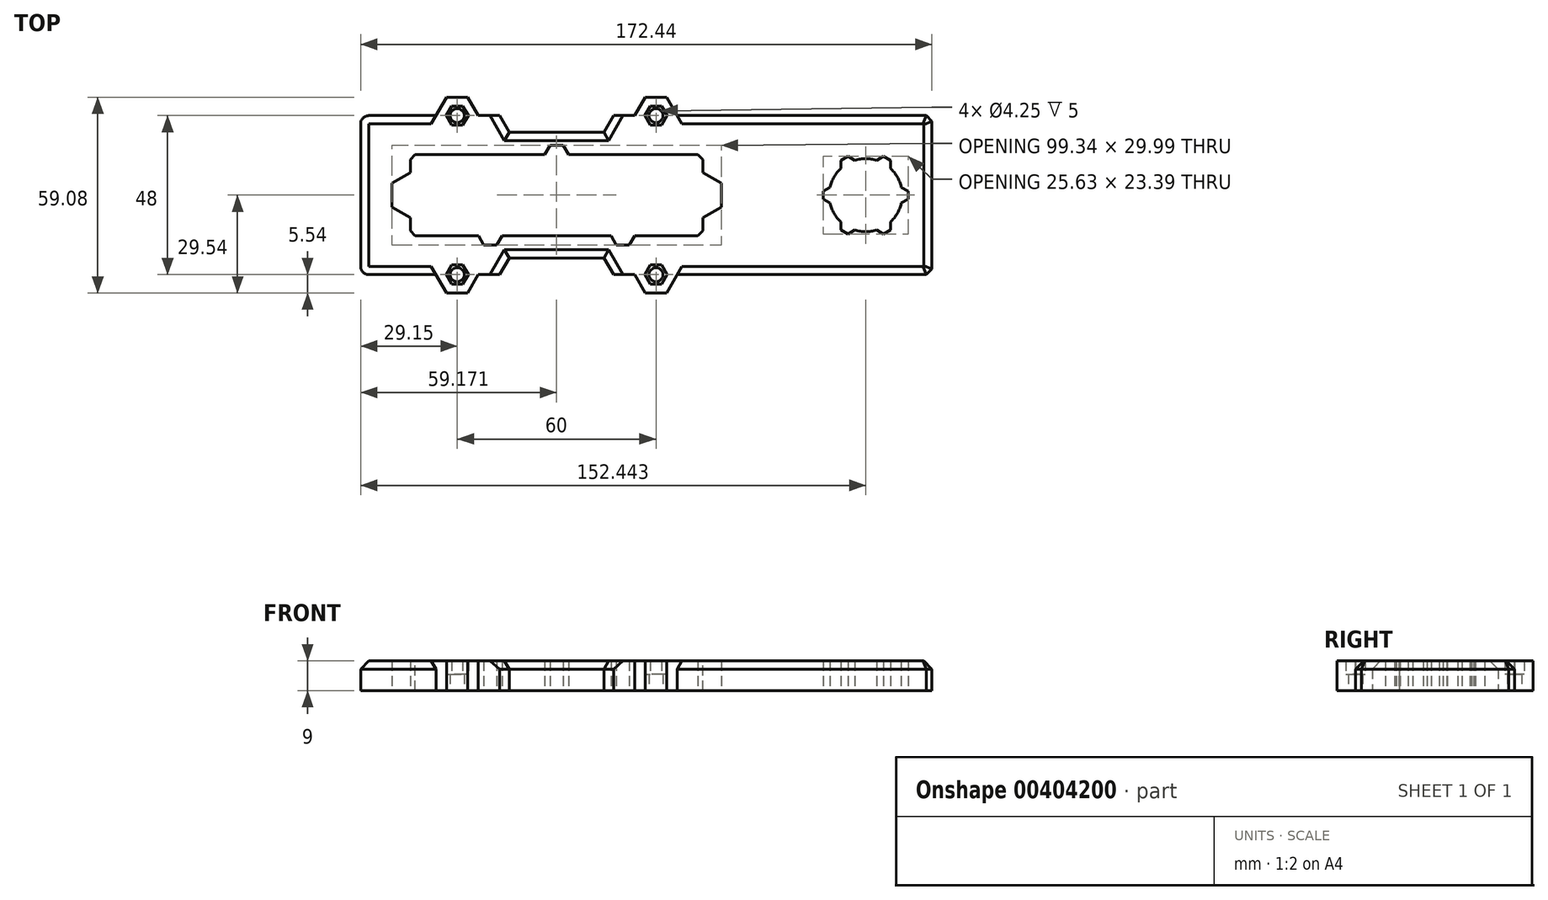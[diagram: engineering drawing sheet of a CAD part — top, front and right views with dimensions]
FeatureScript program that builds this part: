
annotation { "Feature Type Name" : "Feature", "Feature Type Description" : "" }
export const myFeature = defineFeature(function(context is Context, id is Id, definition is map)
    precondition{}
    {
        {
            var Q0;
            Q0=qCreatedBy(makeId("Top.planeOp"),FACE);
            var sketch = newSketch(context, id + "F0", { "sketchPlane" : qUnion([Q0])});
            skLineSegment(sketch, "E0.bottom", {"start": v(37.5, 8.37) * mm, "end": v(-37.5, 8.37) * mm, "construction": true});
            skLineSegment(sketch, "E0.top", {"start": v(37.5, -8.37) * mm, "end": v(-37.5, -8.37) * mm, "construction": true});
            skLineSegment(sketch, "E0.left", {"start": v(37.5, 8.37) * mm, "end": v(37.5, -8.37) * mm, "construction": true});
            skLineSegment(sketch, "E0.right", {"start": v(-37.5, 8.37) * mm, "end": v(-37.5, -8.37) * mm, "construction": true});
            skPoint(sketch, "E0.middle", {"position": v(0, 0) * mm});
            skLineSegment(sketch, "E1.bottom", {"start": v(43.5, 11.57) * mm, "end": v(2.77, 11.57) * mm, "construction": true});
            skLineSegment(sketch, "E1.top", {"start": v(43.5, -11.57) * mm, "end": v(23.2, -11.57) * mm, "construction": true});
            skLineSegment(sketch, "E1.left", {"start": v(43.5, 11.57) * mm, "end": v(43.5, 5.54) * mm, "construction": true});
            skLineSegment(sketch, "E1.right", {"start": v(-43.5, 11.57) * mm, "end": v(-43.5, 6.4) * mm, "construction": true});
            skCircle(sketch, "E2.cCircle", {"center": v(43.5, 0) * mm, "radius": 5.54 * mm, "construction": true});
            skPoint(sketch, "E2.cCircle.centerSnap0", {"position": v(43.5, 0) * mm});
            skLineSegment(sketch, "E2.0", {"start": v(49.04, 3.2) * mm, "end": v(49.04, -3.2) * mm, "construction": true});
            skLineSegment(sketch, "E2.1", {"start": v(49.04, -3.2) * mm, "end": v(43.5, -6.4) * mm, "construction": true});
            skLineSegment(sketch, "E2.2", {"start": v(43.5, -6.4) * mm, "end": v(37.96, -3.2) * mm, "construction": true});
            skLineSegment(sketch, "E2.3", {"start": v(37.96, -3.2) * mm, "end": v(37.96, 3.2) * mm, "construction": true});
            skLineSegment(sketch, "E2.4", {"start": v(37.96, 3.2) * mm, "end": v(43.5, 6.4) * mm, "construction": true});
            skLineSegment(sketch, "E2.5", {"start": v(43.5, 6.4) * mm, "end": v(49.04, 3.2) * mm, "construction": true});
            skPoint(sketch, "E2.0.midPoint", {"position": v(49.04, 0) * mm});
            skLineSegment(sketch, "E3.MirrorCS", {"start": v(-43.5, 6.4) * mm, "end": v(-49.04, 3.2) * mm, "construction": true});
            skLineSegment(sketch, "E4.MirrorCS", {"start": v(-49.04, 3.2) * mm, "end": v(-49.04, -3.2) * mm, "construction": true});
            skLineSegment(sketch, "E5.MirrorCS", {"start": v(-49.04, -3.2) * mm, "end": v(-43.5, -6.4) * mm, "construction": true});
            skLineSegment(sketch, "E6.trimOffspring", {"start": v(-43.5, -6.4) * mm, "end": v(-43.5, -11.57) * mm, "construction": true});
            skLineSegment(sketch, "E7.trimOffspring", {"start": v(43.5, -5.54) * mm, "end": v(43.5, -11.57) * mm, "construction": true});
            skCircle(sketch, "E8.cCircle", {"center": v(0, 11.57) * mm, "radius": 2.77 * mm, "construction": true});
            skLineSegment(sketch, "E8.0", {"start": v(-1.6, 14.35) * mm, "end": v(1.6, 14.35) * mm, "construction": true});
            skLineSegment(sketch, "E8.1", {"start": v(1.6, 14.35) * mm, "end": v(3.2, 11.57) * mm, "construction": true});
            skLineSegment(sketch, "E8.2", {"start": v(3.2, 11.57) * mm, "end": v(1.6, 8.8) * mm, "construction": true});
            skLineSegment(sketch, "E8.3", {"start": v(1.6, 8.8) * mm, "end": v(-1.6, 8.8) * mm, "construction": true});
            skLineSegment(sketch, "E8.4", {"start": v(-1.6, 8.8) * mm, "end": v(-3.2, 11.57) * mm, "construction": true});
            skLineSegment(sketch, "E8.5", {"start": v(-3.2, 11.57) * mm, "end": v(-1.6, 14.35) * mm, "construction": true});
            skPoint(sketch, "E8.0.midPoint", {"position": v(0, 14.35) * mm});
            skCircle(sketch, "E9.cCircle", {"center": v(-20, -11.57) * mm, "radius": 2.77 * mm, "construction": true});
            skLineSegment(sketch, "E9.0", {"start": v(-18.4, -14.35) * mm, "end": v(-21.6, -14.35) * mm, "construction": true});
            skLineSegment(sketch, "E9.1", {"start": v(-21.6, -14.35) * mm, "end": v(-23.2, -11.57) * mm, "construction": true});
            skLineSegment(sketch, "E9.2", {"start": v(-23.2, -11.57) * mm, "end": v(-21.6, -8.8) * mm, "construction": true});
            skLineSegment(sketch, "E9.3", {"start": v(-21.6, -8.8) * mm, "end": v(-18.4, -8.8) * mm, "construction": true});
            skLineSegment(sketch, "E9.4", {"start": v(-18.4, -8.8) * mm, "end": v(-16.8, -11.57) * mm, "construction": true});
            skLineSegment(sketch, "E9.5", {"start": v(-16.8, -11.57) * mm, "end": v(-18.4, -14.35) * mm, "construction": true});
            skPoint(sketch, "E9.0.midPoint", {"position": v(-20, -14.35) * mm});
            skLineSegment(sketch, "E10.MirrorCS", {"start": v(16.8, -11.57) * mm, "end": v(18.4, -14.35) * mm, "construction": true});
            skLineSegment(sketch, "E11.MirrorCS", {"start": v(21.6, -14.35) * mm, "end": v(23.2, -11.57) * mm, "construction": true});
            skLineSegment(sketch, "E12.MirrorCS", {"start": v(18.4, -14.35) * mm, "end": v(21.6, -14.35) * mm, "construction": true});
            skLineSegment(sketch, "E13.trimOffspring", {"start": v(16.8, -11.57) * mm, "end": v(-17.23, -11.57) * mm, "construction": true});
            skLineSegment(sketch, "E14.trimOffspring", {"start": v(-22.77, -11.57) * mm, "end": v(-43.5, -11.57) * mm, "construction": true});
            skLineSegment(sketch, "E15.trimOffspring", {"start": v(-2.77, 11.57) * mm, "end": v(-43.5, 11.57) * mm, "construction": true});
            skCircle(sketch, "E16", {"center": v(43.5, 0) * mm, "radius": 2.25 * mm, "construction": true});
            skCircle(sketch, "E17.MirrorC", {"center": v(-43.5, 0) * mm, "radius": 2.25 * mm, "construction": true});
            skLineSegment(sketch, "E18", {"start": v(0, 15) * mm, "end": v(-1.98, 15) * mm});
            skLineSegment(sketch, "E19", {"start": v(-1.98, 15) * mm, "end": v(-3.58, 12.22) * mm});
            skLineSegment(sketch, "E20", {"start": v(-3.58, 12.22) * mm, "end": v(-44.15, 12.22) * mm});
            skLineSegment(sketch, "E21", {"start": v(-44.15, 12.22) * mm, "end": v(-44.15, 6.78) * mm});
            skLineSegment(sketch, "E22", {"start": v(-44.15, 6.78) * mm, "end": v(-49.7, 3.58) * mm});
            skLineSegment(sketch, "E23", {"start": v(-49.7, 3.58) * mm, "end": v(-49.7, 0) * mm});
            skLineSegment(sketch, "E24.MirrorCS", {"start": v(0, 15) * mm, "end": v(1.98, 15) * mm});
            skLineSegment(sketch, "E25.MirrorCS", {"start": v(1.98, 15) * mm, "end": v(3.58, 12.22) * mm});
            skLineSegment(sketch, "E26.MirrorCS", {"start": v(3.58, 12.22) * mm, "end": v(44.15, 12.22) * mm});
            skLineSegment(sketch, "E27.MirrorCS", {"start": v(44.15, 12.22) * mm, "end": v(44.15, 6.78) * mm});
            skLineSegment(sketch, "E28.MirrorCS", {"start": v(44.15, 6.78) * mm, "end": v(49.7, 3.58) * mm});
            skLineSegment(sketch, "E29.MirrorCS", {"start": v(49.7, 3.58) * mm, "end": v(49.7, 0) * mm});
            skLineSegment(sketch, "E30.MirrorCS", {"start": v(-49.7, -3.58) * mm, "end": v(-49.7, 0) * mm});
            skLineSegment(sketch, "E31.MirrorCS", {"start": v(-44.15, -6.78) * mm, "end": v(-49.7, -3.58) * mm});
            skLineSegment(sketch, "E32.MirrorCS", {"start": v(-44.15, -12.22) * mm, "end": v(-44.15, -6.78) * mm});
            skLineSegment(sketch, "E33.MirrorCS", {"start": v(-3.58, -12.22) * mm, "end": v(-16.42, -12.22) * mm});
            skLineSegment(sketch, "E34.MirrorCS", {"start": v(-1.98, -15) * mm, "end": v(-3.58, -12.22) * mm, "construction": true});
            skLineSegment(sketch, "E35.MirrorCS", {"start": v(0, -15) * mm, "end": v(-1.98, -15) * mm, "construction": true});
            skLineSegment(sketch, "E36.MirrorCS", {"start": v(0, -15) * mm, "end": v(1.98, -15) * mm, "construction": true});
            skLineSegment(sketch, "E37.MirrorCS", {"start": v(1.98, -15) * mm, "end": v(3.58, -12.22) * mm, "construction": true});
            skLineSegment(sketch, "E38.MirrorCS", {"start": v(3.58, -12.22) * mm, "end": v(16.42, -12.22) * mm});
            skLineSegment(sketch, "E39.MirrorCS", {"start": v(44.15, -12.22) * mm, "end": v(44.15, -6.78) * mm});
            skLineSegment(sketch, "E40.MirrorCS", {"start": v(44.15, -6.78) * mm, "end": v(49.7, -3.58) * mm});
            skLineSegment(sketch, "E41.MirrorCS", {"start": v(49.7, -3.58) * mm, "end": v(49.7, 0) * mm});
            skLineSegment(sketch, "E42", {"start": v(-23.58, -12.23) * mm, "end": v(-21.98, -15) * mm});
            skLineSegment(sketch, "E43", {"start": v(-21.98, -15) * mm, "end": v(-18.02, -15) * mm});
            skLineSegment(sketch, "E44", {"start": v(-18.02, -15) * mm, "end": v(-16.42, -12.23) * mm});
            skLineSegment(sketch, "E45.MirrorCS", {"start": v(18.02, -15) * mm, "end": v(16.42, -12.23) * mm});
            skLineSegment(sketch, "E46.MirrorCS", {"start": v(23.58, -12.23) * mm, "end": v(21.98, -15) * mm});
            skLineSegment(sketch, "E47.MirrorCS", {"start": v(21.98, -15) * mm, "end": v(18.02, -15) * mm});
            skLineSegment(sketch, "E48", {"start": v(-3.58, -12.22) * mm, "end": v(3.58, -12.22) * mm});
            skLineSegment(sketch, "E49.trimOffspring", {"start": v(-23.58, -12.22) * mm, "end": v(-44.15, -12.22) * mm});
            skLineSegment(sketch, "E50.trimOffspring", {"start": v(23.58, -12.22) * mm, "end": v(44.15, -12.22) * mm});
            skLineSegment(sketch, "E51", {"start": v(0, -14.23) * mm, "end": v(-15.27, -14.23) * mm});
            skLineSegment(sketch, "E52", {"start": v(-15.27, -14.23) * mm, "end": v(-16.87, -17) * mm});
            skLineSegment(sketch, "E53", {"start": v(-16.87, -17) * mm, "end": v(-23.13, -17) * mm});
            skLineSegment(sketch, "E54", {"start": v(-23.13, -17) * mm, "end": v(-24.73, -14.23) * mm});
            skLineSegment(sketch, "E55", {"start": v(-24.73, -14.23) * mm, "end": v(-46.15, -14.23) * mm});
            skLineSegment(sketch, "E56", {"start": v(-46.15, -14.23) * mm, "end": v(-46.15, -7.93) * mm, "construction": true});
            skLineSegment(sketch, "E57", {"start": v(-46.15, -7.93) * mm, "end": v(-51.7, -4.73) * mm, "construction": true});
            skLineSegment(sketch, "E58", {"start": v(-51.7, -4.73) * mm, "end": v(-51.7, 4.73) * mm, "construction": true});
            skLineSegment(sketch, "E59", {"start": v(-51.7, 4.73) * mm, "end": v(-46.15, 7.93) * mm, "construction": true});
            skLineSegment(sketch, "E60", {"start": v(-46.15, 7.93) * mm, "end": v(-46.15, 14.22) * mm, "construction": true});
            skLineSegment(sketch, "E61", {"start": v(-46.15, 14.22) * mm, "end": v(-4.73, 14.22) * mm});
            skLineSegment(sketch, "E62", {"start": v(-4.73, 14.22) * mm, "end": v(-3.13, 17) * mm});
            skLineSegment(sketch, "E63", {"start": v(-3.13, 17) * mm, "end": v(0, 17) * mm});
            skLineSegment(sketch, "E64.MirrorCS", {"start": v(0, -14.23) * mm, "end": v(15.27, -14.23) * mm});
            skLineSegment(sketch, "E65.MirrorCS", {"start": v(15.27, -14.23) * mm, "end": v(16.87, -17) * mm});
            skLineSegment(sketch, "E66.MirrorCS", {"start": v(16.87, -17) * mm, "end": v(23.13, -17) * mm});
            skLineSegment(sketch, "E67.MirrorCS", {"start": v(23.13, -17) * mm, "end": v(24.73, -14.23) * mm});
            skLineSegment(sketch, "E68.MirrorCS", {"start": v(24.73, -14.23) * mm, "end": v(46.15, -14.23) * mm});
            skLineSegment(sketch, "E69.MirrorCS", {"start": v(46.15, -14.23) * mm, "end": v(46.15, -7.93) * mm});
            skLineSegment(sketch, "E70.MirrorCS", {"start": v(46.15, -7.93) * mm, "end": v(51.7, -4.73) * mm});
            skLineSegment(sketch, "E71.MirrorCS", {"start": v(51.7, -4.73) * mm, "end": v(51.7, 4.73) * mm});
            skLineSegment(sketch, "E72.MirrorCS", {"start": v(51.7, 4.73) * mm, "end": v(46.15, 7.93) * mm});
            skLineSegment(sketch, "E73.MirrorCS", {"start": v(46.15, 7.93) * mm, "end": v(46.15, 14.22) * mm});
            skLineSegment(sketch, "E74.MirrorCS", {"start": v(46.15, 14.22) * mm, "end": v(4.73, 14.22) * mm});
            skLineSegment(sketch, "E75.MirrorCS", {"start": v(4.73, 14.22) * mm, "end": v(3.13, 17) * mm});
            skLineSegment(sketch, "E76.MirrorCS", {"start": v(3.13, 17) * mm, "end": v(0, 17) * mm});
            skLineSegment(sketch, "E77", {"start": v(-46.15, 14.22) * mm, "end": v(-54.15, 14.22) * mm});
            skLineSegment(sketch, "E78", {"start": v(-54.15, 14.22) * mm, "end": v(-54.15, -14.23) * mm});
            skLineSegment(sketch, "E79", {"start": v(-54.15, -14.23) * mm, "end": v(-46.15, -14.23) * mm});
            skSolve(sketch);
        }
        {
            var Q0;
            Q0=qSketchRegion(id+"F0",true);
            extrude(context, id + "F1", {"entities" : qUnion([Q0]), "depth" : 36.5 * mm});
        }
        {
            var Q0;
            Q0=makeQuery(id+"F1.opExtrude","SWEPT_EDGE",EDGE,{"disambiguationData":[OSD([sQuery(id+"F0.wireOp",EDGE,"E20"),sQuery(id+"F0.wireOp",EDGE,"E21")])]});
            var Q1;
            Q1=makeQuery(id+"F1.opExtrude","SWEPT_EDGE",EDGE,{"disambiguationData":[OSD([sQuery(id+"F0.wireOp",EDGE,"E26.MirrorCS"),sQuery(id+"F0.wireOp",EDGE,"E27.MirrorCS")])]});
            var Q2;
            Q2=makeQuery(id+"F1.opExtrude","SWEPT_EDGE",EDGE,{"disambiguationData":[OSD([sQuery(id+"F0.wireOp",EDGE,"E39.MirrorCS"),sQuery(id+"F0.wireOp",EDGE,"E50.trimOffspring")])]});
            var Q3;
            Q3=makeQuery(id+"F1.opExtrude","SWEPT_EDGE",EDGE,{"disambiguationData":[OSD([sQuery(id+"F0.wireOp",EDGE,"E32.MirrorCS"),sQuery(id+"F0.wireOp",EDGE,"E49.trimOffspring")])]});
            chamfer(context, id + "F2", {"entities" : qUnion([Q0, Q1, Q2, Q3]), "width" : 1.5 * mm, "tangentPropagation" : true});
        }
        {
            var Q0;
            Q0=qCreatedBy(makeId("Right.planeOp"),FACE);
            var sketch = newSketch(context, id + "F3", { "sketchPlane" : qUnion([Q0])});
            skArc(sketch, "E80", {"start": v(-11, 32.75) * mm, "mid": v(0, 21.75) * mm, "end": v(11, 32.75) * mm});
            skLineSegment(sketch, "E81", {"start": v(-11, 32.75) * mm, "end": v(-11, 36.5) * mm});
            skLineSegment(sketch, "E82", {"start": v(-11, 36.5) * mm, "end": v(-10.34, 36.5) * mm});
            skLineSegment(sketch, "E83.MirrorCS", {"start": v(11, 32.75) * mm, "end": v(11, 36.5) * mm});
            skArc(sketch, "E84.trimOffspring", {"start": v(10.34, 36.5) * mm, "mid": v(0, 43.75) * mm, "end": v(-10.34, 36.5) * mm});
            skLineSegment(sketch, "E85", {"start": v(10.34, 36.5) * mm, "end": v(11, 36.5) * mm});
            skSolve(sketch);
        }
        {
            var Q0;
            Q0=qSketchRegion(id+"F3",true);
            extrude(context, id + "F4", {"entities" : qUnion([Q0]), "operationType" : NewBodyOperationType.REMOVE, "endBound" : BoundingType.SYMMETRIC, "oppositeDirection" : true, "depth" : 150 * mm});
        }
        {
            var Q0;
            Q0=makeQuery(id+"F1.opExtrude","SWEPT_FACE",FACE,{"disambiguationData":[OSD([sQuery(id+"F0.wireOp",EDGE,"E78")])]});
            var sketch = newSketch(context, id + "F5", { "sketchPlane" : qUnion([Q0])});
            skLineSegment(sketch, "E86", {"start": v(-14.22, 36.5) * mm, "end": v(-14.22, 0) * mm, "construction": true});
            skLineSegment(sketch, "E87", {"start": v(-14.22, 0) * mm, "end": v(14.23, 0) * mm});
            skLineSegment(sketch, "E88", {"start": v(14.23, 0) * mm, "end": v(14.23, 36.5) * mm, "construction": true});
            skArc(sketch, "E89", {"start": v(11, 32.75) * mm, "mid": v(0, 21.75) * mm, "end": v(-11, 32.75) * mm});
            skCircle(sketch, "E90.cCircle", {"center": v(18, 14.75) * mm, "radius": 2.92 * mm, "construction": true});
            skLineSegment(sketch, "E90.0", {"start": v(20.92, 16.43) * mm, "end": v(20.92, 13.07) * mm});
            skLineSegment(sketch, "E90.1", {"start": v(20.92, 13.07) * mm, "end": v(18, 11.38) * mm});
            skLineSegment(sketch, "E90.2", {"start": v(18, 11.38) * mm, "end": v(15.08, 13.07) * mm});
            skLineSegment(sketch, "E90.3", {"start": v(15.08, 13.07) * mm, "end": v(15.08, 16.43) * mm});
            skLineSegment(sketch, "E90.4", {"start": v(15.08, 16.43) * mm, "end": v(18, 18.12) * mm});
            skLineSegment(sketch, "E90.5", {"start": v(18, 18.12) * mm, "end": v(20.92, 16.43) * mm});
            skPoint(sketch, "E90.0.midPoint", {"position": v(20.92, 14.75) * mm});
            skLineSegment(sketch, "E91.MirrorCS", {"start": v(-15.08, 13.07) * mm, "end": v(-15.08, 16.43) * mm});
            skLineSegment(sketch, "E92.MirrorCS", {"start": v(-18, 11.38) * mm, "end": v(-15.08, 13.07) * mm});
            skLineSegment(sketch, "E93.MirrorCS", {"start": v(-20.92, 13.07) * mm, "end": v(-18, 11.38) * mm});
            skLineSegment(sketch, "E94.MirrorCS", {"start": v(-20.92, 16.43) * mm, "end": v(-20.92, 13.07) * mm});
            skCircle(sketch, "E95.MirrorC", {"center": v(-18, 14.75) * mm, "radius": 2.92 * mm, "construction": true});
            skLineSegment(sketch, "E96.MirrorCS", {"start": v(-15.08, 16.43) * mm, "end": v(-18, 18.12) * mm});
            skLineSegment(sketch, "E97.MirrorCS", {"start": v(-18, 18.12) * mm, "end": v(-20.92, 16.43) * mm});
            skPoint(sketch, "E98.MirrorP", {"position": v(-20.92, 14.75) * mm});
            skLineSegment(sketch, "E99", {"start": v(-14.22, 0) * mm, "end": v(-24, 0) * mm});
            skLineSegment(sketch, "E100", {"start": v(-24, 0) * mm, "end": v(-24, 32.75) * mm});
            skLineSegment(sketch, "E101.MirrorCS", {"start": v(24, 0) * mm, "end": v(24, 32.75) * mm});
            skLineSegment(sketch, "E102.MirrorCS", {"start": v(14.22, 0) * mm, "end": v(24, 0) * mm});
            skArc(sketch, "E103", {"start": v(11, 32.75) * mm, "mid": v(0, 43.75) * mm, "end": v(-11, 32.75) * mm});
            skCircle(sketch, "E104.cCircle", {"center": v(0, 50.75) * mm, "radius": 2.92 * mm, "construction": true});
            skLineSegment(sketch, "E104.0", {"start": v(2.92, 52.43) * mm, "end": v(2.92, 49.07) * mm});
            skLineSegment(sketch, "E104.1", {"start": v(2.92, 49.07) * mm, "end": v(0, 47.38) * mm});
            skLineSegment(sketch, "E104.2", {"start": v(0, 47.38) * mm, "end": v(-2.92, 49.07) * mm});
            skLineSegment(sketch, "E104.3", {"start": v(-2.92, 49.07) * mm, "end": v(-2.92, 52.43) * mm});
            skLineSegment(sketch, "E104.4", {"start": v(-2.92, 52.43) * mm, "end": v(0, 54.12) * mm});
            skLineSegment(sketch, "E104.5", {"start": v(0, 54.12) * mm, "end": v(2.92, 52.43) * mm});
            skPoint(sketch, "E104.0.midPoint", {"position": v(2.92, 50.75) * mm});
            skArc(sketch, "E105", {"start": v(24, 32.75) * mm, "mid": v(0, 56.75) * mm, "end": v(-24, 32.75) * mm});
            skSolve(sketch);
        }
        {
            var Q0;
            Q0=qSketchRegion(id+"F5",true);
            extrude(context, id + "F6", {"entities" : qUnion([Q0]), "operationType" : NewBodyOperationType.ADD, "oppositeDirection" : true, "depth" : 4.5 * mm});
        }
        {
            var Q0;
            {var subQ0=sQuery(id+"F5.wireOp",EDGE,"E90.3");var subQ1=sQuery(id+"F5.wireOp",EDGE,"E90.2");var subQ2=sQuery(id+"F5.wireOp",EDGE,"E90.0");var subQ3=sQuery(id+"F5.wireOp",EDGE,"21dbecbc-3e90-4e6d-8c2d-dcc7a88c41760.MirrorCS");var subQ4=sQuery(id+"F5.wireOp",EDGE,"7LxXvKuB-2ogT-G9F5-G1mv-J76seeRdzQWf");var subQ5=sQuery(id+"F5.wireOp",EDGE,"E90.4");var subQ59=sQuery(id+"F5.wireOp",EDGE,"E90.1");var subQ60=sQuery(id+"F5.wireOp",EDGE,"E102.MirrorCS");var subQ61=sQuery(id+"F5.wireOp",EDGE,"E99");var subQ62=sQuery(id+"F5.wireOp",EDGE,"E87");var subQ63=sQuery(id+"F5.wireOp",EDGE,"E101.MirrorCS");var subQ64=sQuery(id+"F5.wireOp",EDGE,"E90.5");Q0=makeQuery(id+"F6.boolean.opBoolean","SPLIT",FACE,{"disambiguationData":[TD([makeQuery(id+"F6.opExtrude","SWEPT_FACE",FACE,{"disambiguationData":[OSD([subQ2])]})])],"derivedFrom":makeQuery(id+"F6.opExtrude","CAP_FACE",FACE,{"disambiguationData":[OSD([sQuery(id+"F5.wireOp",EDGE,"b1FAA0cU-aVsy-Hviu-uORb-ThKFGoumFDh2"),sQuery(id+"F5.wireOp",EDGE,"2LK7XLYA-R4sY-Yq1R-9r0a-fteJpxcb9tpt"),subQ62,subQ4,sQuery(id+"F5.wireOp",EDGE,"kGSWCWjE-YfoX-ZzYT-cJHE-sSvaP37tbrIv"),sQuery(id+"F5.wireOp",EDGE,"E89"),subQ2,subQ59,subQ1,subQ0,subQ5,subQ64,sQuery(id+"F5.wireOp",EDGE,"E91.MirrorCS"),sQuery(id+"F5.wireOp",EDGE,"E92.MirrorCS"),sQuery(id+"F5.wireOp",EDGE,"E93.MirrorCS"),sQuery(id+"F5.wireOp",EDGE,"E94.MirrorCS"),sQuery(id+"F5.wireOp",EDGE,"E96.MirrorCS"),sQuery(id+"F5.wireOp",EDGE,"E97.MirrorCS"),subQ61,sQuery(id+"F5.wireOp",EDGE,"E100"),sQuery(id+"F5.wireOp",EDGE,"KSvhVgnx-WBJf-5fod-QVyl-tOGzJuIU2zdj"),subQ3,subQ63,subQ60])],"isStart":false})});}
            var sketch = newSketch(context, id + "F7", { "sketchPlane" : qUnion([Q0])});
            skCircle(sketch, "E106.cCircle", {"center": v(-18, 14.75) * mm, "radius": 2.92 * mm, "construction": true});
            skPoint(sketch, "E106.cCircle.perimeterSnap0", {"position": v(-20.92, 14.75) * mm});
            skLineSegment(sketch, "E106.0", {"start": v(-20.92, 13.07) * mm, "end": v(-20.92, 16.43) * mm});
            skLineSegment(sketch, "E106.1", {"start": v(-20.92, 16.43) * mm, "end": v(-18, 18.12) * mm});
            skLineSegment(sketch, "E106.2", {"start": v(-18, 18.12) * mm, "end": v(-15.08, 16.43) * mm});
            skLineSegment(sketch, "E106.3", {"start": v(-15.08, 16.43) * mm, "end": v(-15.08, 13.07) * mm});
            skLineSegment(sketch, "E106.4", {"start": v(-15.08, 13.07) * mm, "end": v(-18, 11.38) * mm, "construction": true});
            skLineSegment(sketch, "E106.5", {"start": v(-18, 11.38) * mm, "end": v(-20.92, 13.07) * mm, "construction": true});
            skPoint(sketch, "E106.0.midPoint", {"position": v(-20.92, 14.75) * mm});
            skPoint(sketch, "E106.0.midPoint.positionSnap0", {"position": v(-20.92, 14.75) * mm});
            skLineSegment(sketch, "E107.MirrorCS", {"start": v(20.92, 13.07) * mm, "end": v(20.92, 16.43) * mm});
            skCircle(sketch, "E108.MirrorC", {"center": v(18, 14.75) * mm, "radius": 2.92 * mm, "construction": true});
            skLineSegment(sketch, "E109.MirrorCS", {"start": v(18, 11.38) * mm, "end": v(20.92, 13.07) * mm, "construction": true});
            skLineSegment(sketch, "E110.MirrorCS", {"start": v(15.08, 13.07) * mm, "end": v(18, 11.38) * mm, "construction": true});
            skLineSegment(sketch, "E111.MirrorCS", {"start": v(15.08, 16.43) * mm, "end": v(15.08, 13.07) * mm});
            skLineSegment(sketch, "E112.MirrorCS", {"start": v(20.92, 16.43) * mm, "end": v(18, 18.12) * mm});
            skPoint(sketch, "E113.MirrorP", {"position": v(20.92, 14.75) * mm});
            skLineSegment(sketch, "E114.MirrorCS", {"start": v(18, 18.12) * mm, "end": v(15.08, 16.43) * mm});
            skLineSegment(sketch, "E115.bottom", {"start": v(-24, 32.75) * mm, "end": v(-14.22, 32.75) * mm});
            skLineSegment(sketch, "E115.top", {"start": v(-24, 0) * mm, "end": v(-20.92, 0) * mm});
            skLineSegment(sketch, "E115.left", {"start": v(-24, 32.75) * mm, "end": v(-24, 0) * mm});
            skLineSegment(sketch, "E115.right", {"start": v(-14.22, 32.75) * mm, "end": v(-14.22, 0) * mm});
            skLineSegment(sketch, "E116.MirrorCS", {"start": v(24, 32.75) * mm, "end": v(14.23, 32.75) * mm});
            skLineSegment(sketch, "E117.MirrorCS", {"start": v(24, 32.75) * mm, "end": v(24, 0) * mm});
            skLineSegment(sketch, "E118.MirrorCS", {"start": v(14.23, 32.75) * mm, "end": v(14.23, 0) * mm});
            skLineSegment(sketch, "E119.MirrorCS", {"start": v(24, 0) * mm, "end": v(20.92, 0) * mm});
            skLineSegment(sketch, "E120", {"start": v(-20.92, 13.07) * mm, "end": v(-20.92, 0) * mm});
            skLineSegment(sketch, "E121", {"start": v(-15.08, 13.07) * mm, "end": v(-15.08, 0) * mm});
            skLineSegment(sketch, "E122.MirrorCS", {"start": v(15.08, 13.07) * mm, "end": v(15.08, 0) * mm});
            skLineSegment(sketch, "E123.MirrorCS", {"start": v(20.92, 13.07) * mm, "end": v(20.92, 0) * mm});
            skLineSegment(sketch, "E124.trimOffspring", {"start": v(-15.08, 0) * mm, "end": v(-14.22, 0) * mm});
            skLineSegment(sketch, "E125.trimOffspring", {"start": v(15.08, 0) * mm, "end": v(14.23, 0) * mm});
            skSolve(sketch);
        }
        {
            var Q0;
            Q0=qSketchRegion(id+"F7",true);
            extrude(context, id + "F8", {"entities" : qUnion([Q0]), "operationType" : NewBodyOperationType.ADD, "depth" : 4 * mm});
        }
        {
            var Q0;
            Q0=makeQuery(id+"F6.boolean.opBoolean","MERGE",FACE,{"derivedFrom":[makeQuery(id+"F1.opExtrude","SWEPT_FACE",FACE,{"disambiguationData":[OSD([sQuery(id+"F0.wireOp",EDGE,"E78")])]}),makeQuery(id+"F6.opExtrude","CAP_FACE",FACE,{"disambiguationData":[OSD([sQuery(id+"F5.wireOp",EDGE,"b1FAA0cU-aVsy-Hviu-uORb-ThKFGoumFDh2"),sQuery(id+"F5.wireOp",EDGE,"2LK7XLYA-R4sY-Yq1R-9r0a-fteJpxcb9tpt"),sQuery(id+"F5.wireOp",EDGE,"E87"),sQuery(id+"F5.wireOp",EDGE,"7LxXvKuB-2ogT-G9F5-G1mv-J76seeRdzQWf"),sQuery(id+"F5.wireOp",EDGE,"kGSWCWjE-YfoX-ZzYT-cJHE-sSvaP37tbrIv"),sQuery(id+"F5.wireOp",EDGE,"E89"),sQuery(id+"F5.wireOp",EDGE,"E90.0"),sQuery(id+"F5.wireOp",EDGE,"E90.1"),sQuery(id+"F5.wireOp",EDGE,"E90.2"),sQuery(id+"F5.wireOp",EDGE,"E90.3"),sQuery(id+"F5.wireOp",EDGE,"E90.4"),sQuery(id+"F5.wireOp",EDGE,"E90.5"),sQuery(id+"F5.wireOp",EDGE,"E91.MirrorCS"),sQuery(id+"F5.wireOp",EDGE,"E92.MirrorCS"),sQuery(id+"F5.wireOp",EDGE,"E93.MirrorCS"),sQuery(id+"F5.wireOp",EDGE,"E94.MirrorCS"),sQuery(id+"F5.wireOp",EDGE,"E96.MirrorCS"),sQuery(id+"F5.wireOp",EDGE,"E97.MirrorCS"),sQuery(id+"F5.wireOp",EDGE,"E99"),sQuery(id+"F5.wireOp",EDGE,"E100"),sQuery(id+"F5.wireOp",EDGE,"KSvhVgnx-WBJf-5fod-QVyl-tOGzJuIU2zdj"),sQuery(id+"F5.wireOp",EDGE,"21dbecbc-3e90-4e6d-8c2d-dcc7a88c41760.MirrorCS"),sQuery(id+"F5.wireOp",EDGE,"E101.MirrorCS"),sQuery(id+"F5.wireOp",EDGE,"E102.MirrorCS")])],"isStart":true})]});
            var sketch = newSketch(context, id + "F9", { "sketchPlane" : qUnion([Q0])});
            skCircle(sketch, "E126.cCircle", {"center": v(18, 14.75) * mm, "radius": 2.92 * mm, "construction": true});
            skLineSegment(sketch, "E126.0", {"start": v(20.92, 16.43) * mm, "end": v(20.92, 13.07) * mm});
            skLineSegment(sketch, "E126.1", {"start": v(20.92, 13.07) * mm, "end": v(18, 11.38) * mm, "construction": true});
            skLineSegment(sketch, "E126.2", {"start": v(18, 11.38) * mm, "end": v(15.08, 13.07) * mm, "construction": true});
            skLineSegment(sketch, "E126.3", {"start": v(15.08, 13.07) * mm, "end": v(15.08, 16.43) * mm});
            skLineSegment(sketch, "E126.4", {"start": v(15.08, 16.43) * mm, "end": v(18, 18.12) * mm});
            skLineSegment(sketch, "E126.5", {"start": v(18, 18.12) * mm, "end": v(20.92, 16.43) * mm});
            skPoint(sketch, "E126.0.midPoint", {"position": v(20.92, 14.75) * mm});
            skCircle(sketch, "E127", {"center": v(18, 14.75) * mm, "radius": 2.12 * mm});
            skLineSegment(sketch, "E128.MirrorCS", {"start": v(-20.92, 13.07) * mm, "end": v(-18, 11.38) * mm, "construction": true});
            skPoint(sketch, "E129.MirrorP", {"position": v(-20.92, 14.75) * mm});
            skCircle(sketch, "E130.MirrorC", {"center": v(-18, 14.75) * mm, "radius": 2.92 * mm, "construction": true});
            skCircle(sketch, "E131.MirrorC", {"center": v(-18, 14.75) * mm, "radius": 2.12 * mm});
            skLineSegment(sketch, "E132.MirrorCS", {"start": v(-18, 18.12) * mm, "end": v(-20.92, 16.43) * mm});
            skLineSegment(sketch, "E133.MirrorCS", {"start": v(-15.08, 16.43) * mm, "end": v(-18, 18.12) * mm});
            skLineSegment(sketch, "E134.MirrorCS", {"start": v(-15.08, 13.07) * mm, "end": v(-15.08, 16.43) * mm});
            skLineSegment(sketch, "E135.MirrorCS", {"start": v(-18, 11.38) * mm, "end": v(-15.08, 13.07) * mm, "construction": true});
            skLineSegment(sketch, "E136.MirrorCS", {"start": v(-20.92, 16.43) * mm, "end": v(-20.92, 13.07) * mm});
            skLineSegment(sketch, "E137", {"start": v(20.92, 13.07) * mm, "end": v(20.92, 0) * mm});
            skLineSegment(sketch, "E138", {"start": v(20.92, 0) * mm, "end": v(15.08, 0) * mm});
            skLineSegment(sketch, "E139", {"start": v(15.08, 0) * mm, "end": v(15.08, 13.07) * mm});
            skLineSegment(sketch, "E140.MirrorCS", {"start": v(-15.08, 0) * mm, "end": v(-15.08, 13.07) * mm});
            skLineSegment(sketch, "E141.MirrorCS", {"start": v(-20.92, 13.07) * mm, "end": v(-20.92, 0) * mm});
            skLineSegment(sketch, "E142.MirrorCS", {"start": v(-20.92, 0) * mm, "end": v(-15.08, 0) * mm});
            skSolve(sketch);
        }
        {
            var Q0;
            Q0=qSketchRegion(id+"F9",true);
            extrude(context, id + "F10", {"entities" : qUnion([Q0]), "operationType" : NewBodyOperationType.ADD, "oppositeDirection" : true, "depth" : 4 * mm});
        }
        {
            var Q0;
            {var subQ0=sQuery(id+"F5.wireOp",EDGE,"E100");var subQ1=sQuery(id+"F5.wireOp",EDGE,"E97.MirrorCS");var subQ2=sQuery(id+"F5.wireOp",EDGE,"E96.MirrorCS");var subQ3=sQuery(id+"F5.wireOp",EDGE,"E94.MirrorCS");var subQ4=sQuery(id+"F5.wireOp",EDGE,"E93.MirrorCS");var subQ5=sQuery(id+"F5.wireOp",EDGE,"E92.MirrorCS");var subQ6=sQuery(id+"F5.wireOp",EDGE,"E91.MirrorCS");var subQ7=sQuery(id+"F5.wireOp",EDGE,"E90.5");var subQ8=sQuery(id+"F5.wireOp",EDGE,"E90.4");var subQ9=sQuery(id+"F5.wireOp",EDGE,"E90.3");var subQ10=sQuery(id+"F5.wireOp",EDGE,"E90.2");var subQ11=sQuery(id+"F5.wireOp",EDGE,"E90.1");var subQ14=sQuery(id+"F5.wireOp",EDGE,"E104.0");var subQ73=sQuery(id+"F5.wireOp",EDGE,"E102.MirrorCS");var subQ74=sQuery(id+"F5.wireOp",EDGE,"E99");var subQ75=sQuery(id+"F5.wireOp",EDGE,"E87");var subQ76=sQuery(id+"F5.wireOp",EDGE,"822r9Sqc-ou8d-xyd6-ONRq-5U1WncNYngyn");var subQ77=sQuery(id+"F5.wireOp",EDGE,"E90.0");var subQ78=sQuery(id+"F5.wireOp",EDGE,"E103");var subQ79=sQuery(id+"F5.wireOp",EDGE,"E89");var subQ80=sQuery(id+"F5.wireOp",EDGE,"E101.MirrorCS");var subQ81=sQuery(id+"F5.wireOp",EDGE,"E104.1");var subQ82=sQuery(id+"F5.wireOp",EDGE,"E104.2");var subQ83=sQuery(id+"F5.wireOp",EDGE,"E104.3");var subQ84=sQuery(id+"F5.wireOp",EDGE,"E104.4");var subQ85=sQuery(id+"F5.wireOp",EDGE,"E104.5");Q0=makeQuery(id+"F6.boolean.opBoolean","SPLIT",FACE,{"disambiguationData":[TD([makeQuery(id+"F6.opExtrude","SWEPT_FACE",FACE,{"disambiguationData":[OSD([subQ77])]})])],"derivedFrom":makeQuery(id+"F6.opExtrude","CAP_FACE",FACE,{"disambiguationData":[OSD([subQ75,subQ79,subQ77,subQ11,subQ10,subQ9,subQ8,subQ7,subQ6,subQ5,subQ4,subQ3,subQ2,subQ1,subQ74,subQ0,subQ80,subQ73,subQ78,subQ76,subQ14,subQ81,subQ82,subQ83,subQ84,subQ85])],"isStart":false})});}
            var sketch = newSketch(context, id + "F11", { "sketchPlane" : qUnion([Q0])});
            skArc(sketch, "E143", {"start": v(-11, 32.75) * mm, "mid": v(0, 43.75) * mm, "end": v(11, 32.75) * mm});
            skArc(sketch, "E144", {"start": v(-24, 32.75) * mm, "mid": v(-17.97, 48.66) * mm, "end": v(-2.92, 56.57) * mm});
            skCircle(sketch, "E145.cCircle", {"center": v(0, 50.75) * mm, "radius": 2.92 * mm, "construction": true});
            skPoint(sketch, "E145.cCircle.perimeterSnap0", {"position": v(2.92, 50.75) * mm});
            skLineSegment(sketch, "E145.0", {"start": v(2.92, 52.43) * mm, "end": v(2.92, 49.07) * mm});
            skLineSegment(sketch, "E145.1", {"start": v(2.92, 49.07) * mm, "end": v(0, 47.38) * mm});
            skLineSegment(sketch, "E145.2", {"start": v(0, 47.38) * mm, "end": v(-2.92, 49.07) * mm});
            skLineSegment(sketch, "E145.3", {"start": v(-2.92, 49.07) * mm, "end": v(-2.92, 52.43) * mm});
            skLineSegment(sketch, "E145.4", {"start": v(-2.92, 52.43) * mm, "end": v(0, 54.12) * mm, "construction": true});
            skLineSegment(sketch, "E145.5", {"start": v(0, 54.12) * mm, "end": v(2.92, 52.43) * mm, "construction": true});
            skPoint(sketch, "E145.0.midPoint", {"position": v(2.92, 50.75) * mm});
            skPoint(sketch, "E145.0.midPoint.positionSnap0", {"position": v(2.92, 50.75) * mm});
            skLineSegment(sketch, "E146", {"start": v(-11, 32.75) * mm, "end": v(-24, 32.75) * mm});
            skLineSegment(sketch, "E147", {"start": v(11, 32.75) * mm, "end": v(24, 32.75) * mm});
            skLineSegment(sketch, "E148", {"start": v(-2.92, 56.57) * mm, "end": v(-2.92, 52.43) * mm});
            skLineSegment(sketch, "E149.MirrorCS", {"start": v(2.92, 56.57) * mm, "end": v(2.92, 52.43) * mm});
            skArc(sketch, "E150.trimOffspring", {"start": v(2.92, 56.57) * mm, "mid": v(17.97, 48.66) * mm, "end": v(24, 32.75) * mm});
            skSolve(sketch);
        }
        {
            var Q0;
            Q0=qSketchRegion(id+"F11",true);
            extrude(context, id + "F12", {"entities" : qUnion([Q0]), "operationType" : NewBodyOperationType.ADD, "depth" : 4 * mm});
        }
        {
            var Q0;
            Q0=makeQuery(id+"F10.boolean.opBoolean","MERGE",FACE,{"derivedFrom":[makeQuery(id+"F6.boolean.opBoolean","MERGE",FACE,{"derivedFrom":[makeQuery(id+"F1.opExtrude","SWEPT_FACE",FACE,{"disambiguationData":[OSD([sQuery(id+"F0.wireOp",EDGE,"E78")])]}),makeQuery(id+"F6.opExtrude","CAP_FACE",FACE,{"disambiguationData":[OSD([sQuery(id+"F5.wireOp",EDGE,"E87"),sQuery(id+"F5.wireOp",EDGE,"E89"),sQuery(id+"F5.wireOp",EDGE,"E90.0"),sQuery(id+"F5.wireOp",EDGE,"E90.1"),sQuery(id+"F5.wireOp",EDGE,"E90.2"),sQuery(id+"F5.wireOp",EDGE,"E90.3"),sQuery(id+"F5.wireOp",EDGE,"E90.4"),sQuery(id+"F5.wireOp",EDGE,"E90.5"),sQuery(id+"F5.wireOp",EDGE,"E91.MirrorCS"),sQuery(id+"F5.wireOp",EDGE,"E92.MirrorCS"),sQuery(id+"F5.wireOp",EDGE,"E93.MirrorCS"),sQuery(id+"F5.wireOp",EDGE,"E94.MirrorCS"),sQuery(id+"F5.wireOp",EDGE,"E96.MirrorCS"),sQuery(id+"F5.wireOp",EDGE,"E97.MirrorCS"),sQuery(id+"F5.wireOp",EDGE,"E99"),sQuery(id+"F5.wireOp",EDGE,"E100"),sQuery(id+"F5.wireOp",EDGE,"E101.MirrorCS"),sQuery(id+"F5.wireOp",EDGE,"E102.MirrorCS"),sQuery(id+"F5.wireOp",EDGE,"E103"),sQuery(id+"F5.wireOp",EDGE,"822r9Sqc-ou8d-xyd6-ONRq-5U1WncNYngyn"),sQuery(id+"F5.wireOp",EDGE,"E104.0"),sQuery(id+"F5.wireOp",EDGE,"E104.1"),sQuery(id+"F5.wireOp",EDGE,"E104.2"),sQuery(id+"F5.wireOp",EDGE,"E104.3"),sQuery(id+"F5.wireOp",EDGE,"E104.4"),sQuery(id+"F5.wireOp",EDGE,"E104.5")])],"isStart":true})]}),makeQuery(id+"F10.opExtrude","CAP_FACE",FACE,{"disambiguationData":[OSD([sQuery(id+"F9.wireOp",EDGE,"E126.0"),sQuery(id+"F9.wireOp",EDGE,"E126.1"),sQuery(id+"F9.wireOp",EDGE,"E126.2"),sQuery(id+"F9.wireOp",EDGE,"E126.3"),sQuery(id+"F9.wireOp",EDGE,"E126.4"),sQuery(id+"F9.wireOp",EDGE,"E126.5"),sQuery(id+"F9.wireOp",EDGE,"E127")])],"isStart":true}),makeQuery(id+"F10.opExtrude","CAP_FACE",FACE,{"disambiguationData":[OSD([sQuery(id+"F9.wireOp",EDGE,"E128.MirrorCS"),sQuery(id+"F9.wireOp",EDGE,"E131.MirrorC"),sQuery(id+"F9.wireOp",EDGE,"E132.MirrorCS"),sQuery(id+"F9.wireOp",EDGE,"E133.MirrorCS"),sQuery(id+"F9.wireOp",EDGE,"E134.MirrorCS"),sQuery(id+"F9.wireOp",EDGE,"E135.MirrorCS"),sQuery(id+"F9.wireOp",EDGE,"E136.MirrorCS")])],"isStart":true})]});
            var sketch = newSketch(context, id + "F13", { "sketchPlane" : qUnion([Q0])});
            skCircle(sketch, "E151.cCircle", {"center": v(0, 50.75) * mm, "radius": 2.92 * mm, "construction": true});
            skLineSegment(sketch, "E151.0", {"start": v(2.92, 52.43) * mm, "end": v(2.92, 49.07) * mm});
            skLineSegment(sketch, "E151.1", {"start": v(2.92, 49.07) * mm, "end": v(0, 47.38) * mm});
            skLineSegment(sketch, "E151.2", {"start": v(0, 47.38) * mm, "end": v(-2.92, 49.07) * mm});
            skLineSegment(sketch, "E151.3", {"start": v(-2.92, 49.07) * mm, "end": v(-2.92, 52.43) * mm});
            skLineSegment(sketch, "E151.4", {"start": v(-2.92, 52.43) * mm, "end": v(0, 54.12) * mm});
            skLineSegment(sketch, "E151.5", {"start": v(0, 54.12) * mm, "end": v(2.92, 52.43) * mm});
            skPoint(sketch, "E151.0.midPoint", {"position": v(2.92, 50.75) * mm});
            skCircle(sketch, "E152", {"center": v(0, 50.75) * mm, "radius": 2.12 * mm});
            skSolve(sketch);
        }
        {
            var Q0;
            Q0=qSketchRegion(id+"F13",true);
            extrude(context, id + "F14", {"entities" : qUnion([Q0]), "operationType" : NewBodyOperationType.ADD, "oppositeDirection" : true, "depth" : 4 * mm});
        }
        {
            var Q0;
            {var subQ0=sQuery(id+"F5.wireOp",EDGE,"E90.3");var subQ2=sQuery(id+"F5.wireOp",EDGE,"E90.2");var subQ58=sQuery(id+"F5.wireOp",EDGE,"E102.MirrorCS");var subQ59=sQuery(id+"F5.wireOp",EDGE,"E99");var subQ60=sQuery(id+"F5.wireOp",EDGE,"E87");var subQ62=sQuery(id+"F5.wireOp",EDGE,"E90.0");var subQ63=makeQuery(id+"F6.opExtrude","SWEPT_FACE",FACE,{"disambiguationData":[OSD([subQ62])]});var subQ64=sQuery(id+"F5.wireOp",EDGE,"E90.1");var subQ66=sQuery(id+"F5.wireOp",EDGE,"E100");var subQ67=sQuery(id+"F5.wireOp",EDGE,"E97.MirrorCS");var subQ68=sQuery(id+"F5.wireOp",EDGE,"E96.MirrorCS");var subQ69=sQuery(id+"F5.wireOp",EDGE,"E94.MirrorCS");var subQ70=sQuery(id+"F5.wireOp",EDGE,"E93.MirrorCS");var subQ71=sQuery(id+"F5.wireOp",EDGE,"E92.MirrorCS");var subQ72=sQuery(id+"F5.wireOp",EDGE,"E91.MirrorCS");var subQ73=sQuery(id+"F5.wireOp",EDGE,"E90.5");var subQ74=sQuery(id+"F5.wireOp",EDGE,"E90.4");var subQ75=sQuery(id+"F5.wireOp",EDGE,"E104.1");var subQ83=sQuery(id+"F5.wireOp",EDGE,"E104.0");var subQ84=sQuery(id+"F5.wireOp",EDGE,"E103");var subQ85=sQuery(id+"F5.wireOp",EDGE,"E89");var subQ86=sQuery(id+"F5.wireOp",EDGE,"E101.MirrorCS");var subQ87=sQuery(id+"F5.wireOp",EDGE,"E104.2");var subQ88=sQuery(id+"F5.wireOp",EDGE,"E104.3");var subQ89=sQuery(id+"F5.wireOp",EDGE,"E104.4");var subQ90=sQuery(id+"F5.wireOp",EDGE,"E104.5");var subQ91=sQuery(id+"F5.wireOp",EDGE,"E105");Q0=makeQuery(id+"F8.boolean.opBoolean","SPLIT",FACE,{"disambiguationData":[TD([subQ63])],"derivedFrom":makeQuery(id+"F6.boolean.opBoolean","SPLIT",FACE,{"disambiguationData":[TD([subQ63])],"derivedFrom":makeQuery(id+"F6.opExtrude","CAP_FACE",FACE,{"disambiguationData":[OSD([subQ60,subQ85,subQ62,subQ64,subQ2,subQ0,subQ74,subQ73,subQ72,subQ71,subQ70,subQ69,subQ68,subQ67,subQ59,subQ66,subQ86,subQ58,subQ84,subQ83,subQ75,subQ87,subQ88,subQ89,subQ90,subQ91])],"isStart":false})})});}
            var sketch = newSketch(context, id + "F15", { "sketchPlane" : qUnion([Q0])});
            skCircle(sketch, "E153.cCircle", {"center": v(-18, 14.75) * mm, "radius": 2.92 * mm, "construction": true});
            skLineSegment(sketch, "E153.0", {"start": v(-20.92, 13.07) * mm, "end": v(-20.92, 16.43) * mm});
            skLineSegment(sketch, "E153.1", {"start": v(-20.92, 16.43) * mm, "end": v(-18, 18.12) * mm});
            skLineSegment(sketch, "E153.2", {"start": v(-18, 18.12) * mm, "end": v(-15.08, 16.43) * mm});
            skLineSegment(sketch, "E153.3", {"start": v(-15.08, 16.43) * mm, "end": v(-15.08, 13.07) * mm});
            skLineSegment(sketch, "E153.4", {"start": v(-15.08, 13.07) * mm, "end": v(-18, 11.38) * mm});
            skLineSegment(sketch, "E153.5", {"start": v(-18, 11.38) * mm, "end": v(-20.92, 13.07) * mm});
            skPoint(sketch, "E153.0.midPoint", {"position": v(-20.92, 14.75) * mm});
            skCircle(sketch, "E154", {"center": v(-18, 14.75) * mm, "radius": 2.12 * mm});
            skCircle(sketch, "E155.MirrorC", {"center": v(18, 14.75) * mm, "radius": 2.92 * mm, "construction": true});
            skPoint(sketch, "E156.MirrorP", {"position": v(20.92, 14.75) * mm});
            skLineSegment(sketch, "E157.MirrorCS", {"start": v(20.92, 13.07) * mm, "end": v(20.92, 16.43) * mm});
            skLineSegment(sketch, "E158.MirrorCS", {"start": v(20.92, 16.43) * mm, "end": v(18, 18.12) * mm});
            skLineSegment(sketch, "E159.MirrorCS", {"start": v(18, 18.12) * mm, "end": v(15.08, 16.43) * mm});
            skCircle(sketch, "E160.MirrorC", {"center": v(18, 14.75) * mm, "radius": 2.12 * mm});
            skLineSegment(sketch, "E161.MirrorCS", {"start": v(15.08, 13.07) * mm, "end": v(18, 11.38) * mm});
            skLineSegment(sketch, "E162.MirrorCS", {"start": v(18, 11.38) * mm, "end": v(20.92, 13.07) * mm});
            skLineSegment(sketch, "E163.MirrorCS", {"start": v(15.08, 16.43) * mm, "end": v(15.08, 13.07) * mm});
            skSolve(sketch);
        }
        {
            var Q0;
            Q0=qSketchRegion(id+"F15",true);
            extrude(context, id + "F16", {"entities" : qUnion([Q0]), "operationType" : NewBodyOperationType.ADD, "oppositeDirection" : true, "depth" : 4 * mm});
        }
        {
            var Q0;
            Q0=qCreatedBy(makeId("Top.planeOp"),FACE);
            var sketch = newSketch(context, id + "F17", { "sketchPlane" : qUnion([Q0])});
            skLineSegment(sketch, "E164", {"start": v(-23.13, -17) * mm, "end": v(-24.73, -14.23) * mm});
            skLineSegment(sketch, "E165", {"start": v(-24.73, -14.23) * mm, "end": v(-45.65, -14.23) * mm});
            skLineSegment(sketch, "E166", {"start": v(-45.65, -14.23) * mm, "end": v(-45.65, -24) * mm});
            skLineSegment(sketch, "E167", {"start": v(-45.65, -24) * mm, "end": v(-20.91, -24) * mm});
            skLineSegment(sketch, "E168", {"start": v(-20.91, -24) * mm, "end": v(-16.87, -17) * mm, "construction": true});
            skLineSegment(sketch, "E169", {"start": v(-16.87, -17) * mm, "end": v(-23.13, -17) * mm});
            skLineSegment(sketch, "E170.MirrorCS", {"start": v(-20.91, 24) * mm, "end": v(-16.87, 17) * mm, "construction": true});
            skLineSegment(sketch, "E171.MirrorCS", {"start": v(-45.65, 14.23) * mm, "end": v(-45.65, 24) * mm});
            skLineSegment(sketch, "E172.MirrorCS", {"start": v(-24.73, 14.23) * mm, "end": v(-45.65, 14.23) * mm});
            skLineSegment(sketch, "E173.MirrorCS", {"start": v(-45.65, 24) * mm, "end": v(-20.91, 24) * mm});
            skLineSegment(sketch, "E174.MirrorCS", {"start": v(-16.87, 17) * mm, "end": v(-23.13, 17) * mm, "construction": true});
            skLineSegment(sketch, "E175.MirrorCS", {"start": v(-23.13, 17) * mm, "end": v(-24.73, 14.23) * mm, "construction": true});
            skLineSegment(sketch, "E176", {"start": v(-20.91, -24) * mm, "end": v(46.15, -24) * mm});
            skLineSegment(sketch, "E177", {"start": v(46.15, -24) * mm, "end": v(46.15, -14.22) * mm, "construction": true});
            skLineSegment(sketch, "E178", {"start": v(46.15, -14.22) * mm, "end": v(24.73, -14.22) * mm});
            skLineSegment(sketch, "E179", {"start": v(24.73, -14.23) * mm, "end": v(23.13, -17) * mm});
            skLineSegment(sketch, "E180", {"start": v(23.13, -17) * mm, "end": v(16.87, -17) * mm});
            skLineSegment(sketch, "E181", {"start": v(16.87, -17) * mm, "end": v(15.27, -14.22) * mm});
            skLineSegment(sketch, "E182", {"start": v(15.27, -14.22) * mm, "end": v(-15.27, -14.23) * mm});
            skLineSegment(sketch, "E183", {"start": v(-15.27, -14.23) * mm, "end": v(-16.87, -17) * mm});
            skLineSegment(sketch, "E184", {"start": v(46.15, 14.22) * mm, "end": v(46.15, 24) * mm, "construction": true});
            skLineSegment(sketch, "E185", {"start": v(46.15, 24) * mm, "end": v(-20.91, 24) * mm});
            skLineSegment(sketch, "E186", {"start": v(-24.73, 14.23) * mm, "end": v(-4.73, 14.23) * mm});
            skLineSegment(sketch, "E187", {"start": v(-4.73, 14.23) * mm, "end": v(-3.13, 17) * mm});
            skLineSegment(sketch, "E188", {"start": v(-3.13, 17) * mm, "end": v(3.13, 17) * mm});
            skLineSegment(sketch, "E189", {"start": v(3.13, 17) * mm, "end": v(4.73, 14.22) * mm});
            skLineSegment(sketch, "E190", {"start": v(4.73, 14.22) * mm, "end": v(46.15, 14.23) * mm});
            skLineSegment(sketch, "E191", {"start": v(46.15, -14.22) * mm, "end": v(46.15, -7.93) * mm});
            skLineSegment(sketch, "E192", {"start": v(46.15, -7.93) * mm, "end": v(51.7, -4.73) * mm});
            skLineSegment(sketch, "E193", {"start": v(51.7, -4.73) * mm, "end": v(51.7, 4.73) * mm});
            skLineSegment(sketch, "E194", {"start": v(51.7, 4.73) * mm, "end": v(46.15, 7.93) * mm});
            skLineSegment(sketch, "E195", {"start": v(46.15, 7.93) * mm, "end": v(46.15, 14.22) * mm});
            skLineSegment(sketch, "E196", {"start": v(46.15, -24) * mm, "end": v(53.3, -24) * mm});
            skLineSegment(sketch, "E197", {"start": v(53.3, -24) * mm, "end": v(53.3, 24) * mm});
            skLineSegment(sketch, "E198", {"start": v(53.3, 24) * mm, "end": v(46.15, 24) * mm});
            skSolve(sketch);
        }
        {
            var Q0;
            Q0=qSketchRegion(id+"F17",true);
            extrude(context, id + "F18", {"entities" : qUnion([Q0]), "operationType" : NewBodyOperationType.ADD, "depth" : 32.75 * mm});
        }
        {
            var Q0;
            Q0=makeQuery(id+"F18.opExtrude","SWEPT_FACE",FACE,{"disambiguationData":[OSD([sQuery(id+"F17.wireOp",EDGE,"E197")])]});
            var sketch = newSketch(context, id + "F19", { "sketchPlane" : qUnion([Q0])});
            skArc(sketch, "E199", {"start": v(10.34, 36.5) * mm, "mid": v(0, 43.75) * mm, "end": v(-10.34, 36.5) * mm});
            skLineSegment(sketch, "E200", {"start": v(11, 32.75) * mm, "end": v(11, 36.5) * mm});
            skLineSegment(sketch, "E201", {"start": v(11, 36.5) * mm, "end": v(10.34, 36.5) * mm});
            skLineSegment(sketch, "E202.MirrorCS", {"start": v(-11, 32.75) * mm, "end": v(-11, 36.5) * mm});
            skLineSegment(sketch, "E203.MirrorCS", {"start": v(-11, 36.5) * mm, "end": v(-10.34, 36.5) * mm});
            skArc(sketch, "E204.trimOffspring", {"start": v(-11, 32.75) * mm, "mid": v(0, 21.75) * mm, "end": v(11, 32.75) * mm});
            skSolve(sketch);
        }
        {
            var Q0;
            Q0=qSketchRegion(id+"F19",true);
            extrude(context, id + "F20", {"entities" : qUnion([Q0]), "operationType" : NewBodyOperationType.REMOVE, "oppositeDirection" : true, "depth" : 10 * mm});
        }
        {
            var Q0;
            {var subQ0=sQuery(id+"F5.wireOp",EDGE,"E104.0");var subQ18=sQuery(id+"F5.wireOp",EDGE,"E101.MirrorCS");var subQ20=sQuery(id+"F5.wireOp",EDGE,"E100");var subQ21=makeQuery(id+"F6.opExtrude","SWEPT_FACE",FACE,{"disambiguationData":[OSD([subQ20])]});var subQ22=sQuery(id+"F5.wireOp",EDGE,"E103");var subQ23=sQuery(id+"F5.wireOp",EDGE,"E89");var subQ71=sQuery(id+"F5.wireOp",EDGE,"E104.5");var subQ74=sQuery(id+"F5.wireOp",EDGE,"E104.3");var subQ78=sQuery(id+"F5.wireOp",EDGE,"E104.1");var subQ80=sQuery(id+"F5.wireOp",EDGE,"E104.2");var subQ82=sQuery(id+"F5.wireOp",EDGE,"E104.4");var subQ84=sQuery(id+"F5.wireOp",EDGE,"E105");var subQ86=sQuery(id+"F5.wireOp",EDGE,"E97.MirrorCS");var subQ87=sQuery(id+"F5.wireOp",EDGE,"E96.MirrorCS");var subQ88=sQuery(id+"F5.wireOp",EDGE,"E94.MirrorCS");var subQ89=sQuery(id+"F5.wireOp",EDGE,"E93.MirrorCS");var subQ90=sQuery(id+"F5.wireOp",EDGE,"E92.MirrorCS");var subQ91=sQuery(id+"F5.wireOp",EDGE,"E91.MirrorCS");var subQ92=sQuery(id+"F5.wireOp",EDGE,"E90.5");var subQ93=sQuery(id+"F5.wireOp",EDGE,"E90.4");var subQ94=sQuery(id+"F5.wireOp",EDGE,"E90.3");var subQ95=sQuery(id+"F5.wireOp",EDGE,"E90.2");var subQ96=sQuery(id+"F5.wireOp",EDGE,"E90.1");var subQ97=sQuery(id+"F5.wireOp",EDGE,"E102.MirrorCS");var subQ98=sQuery(id+"F5.wireOp",EDGE,"E99");var subQ99=sQuery(id+"F5.wireOp",EDGE,"E87");var subQ100=sQuery(id+"F5.wireOp",EDGE,"E90.0");Q0=makeQuery(id+"F8.boolean.opBoolean","SPLIT",FACE,{"disambiguationData":[TD([subQ21])],"derivedFrom":makeQuery(id+"F6.boolean.opBoolean","SPLIT",FACE,{"disambiguationData":[TD([makeQuery(id+"F6.opExtrude","SWEPT_FACE",FACE,{"disambiguationData":[OSD([subQ100])]})])],"derivedFrom":makeQuery(id+"F6.opExtrude","CAP_FACE",FACE,{"disambiguationData":[OSD([subQ99,subQ23,subQ100,subQ96,subQ95,subQ94,subQ93,subQ92,subQ91,subQ90,subQ89,subQ88,subQ87,subQ86,subQ98,subQ20,subQ18,subQ97,subQ22,subQ0,subQ78,subQ80,subQ74,subQ82,subQ71,subQ84])],"isStart":false})})});}
            var sketch = newSketch(context, id + "F21", { "sketchPlane" : qUnion([Q0])});
            skCircle(sketch, "E205.cCircle", {"center": v(0, 50.75) * mm, "radius": 2.92 * mm, "construction": true});
            skLineSegment(sketch, "E205.0", {"start": v(2.92, 52.43) * mm, "end": v(2.92, 49.07) * mm});
            skLineSegment(sketch, "E205.1", {"start": v(2.92, 49.07) * mm, "end": v(0, 47.38) * mm});
            skLineSegment(sketch, "E205.2", {"start": v(0, 47.38) * mm, "end": v(-2.92, 49.07) * mm});
            skLineSegment(sketch, "E205.3", {"start": v(-2.92, 49.07) * mm, "end": v(-2.92, 52.43) * mm});
            skLineSegment(sketch, "E205.4", {"start": v(-2.92, 52.43) * mm, "end": v(0, 54.12) * mm});
            skLineSegment(sketch, "E205.5", {"start": v(0, 54.12) * mm, "end": v(2.92, 52.43) * mm});
            skPoint(sketch, "E205.0.midPoint", {"position": v(2.92, 50.75) * mm});
            skCircle(sketch, "E206", {"center": v(0, 50.75) * mm, "radius": 2.12 * mm});
            skSolve(sketch);
        }
        {
            var Q0;
            Q0=qSketchRegion(id+"F21",true);
            extrude(context, id + "F22", {"entities" : qUnion([Q0]), "operationType" : NewBodyOperationType.ADD, "oppositeDirection" : true, "depth" : 2 * mm});
        }
        {
            var Q0;
            Q0=makeQuery(id+"F12.boolean.opBoolean","MERGE",FACE,{"derivedFrom":[makeQuery(id+"F8.opExtrude","CAP_FACE",FACE,{"disambiguationData":[OSD([sQuery(id+"F7.wireOp",EDGE,"E106.0"),sQuery(id+"F7.wireOp",EDGE,"E106.1"),sQuery(id+"F7.wireOp",EDGE,"E106.2"),sQuery(id+"F7.wireOp",EDGE,"E106.3"),sQuery(id+"F7.wireOp",EDGE,"E115.bottom"),sQuery(id+"F7.wireOp",EDGE,"E115.top"),sQuery(id+"F7.wireOp",EDGE,"E115.left"),sQuery(id+"F7.wireOp",EDGE,"E115.right"),sQuery(id+"F7.wireOp",EDGE,"E120"),sQuery(id+"F7.wireOp",EDGE,"E121"),sQuery(id+"F7.wireOp",EDGE,"E124.trimOffspring")])],"isStart":false}),makeQuery(id+"F8.opExtrude","CAP_FACE",FACE,{"disambiguationData":[OSD([sQuery(id+"F7.wireOp",EDGE,"E107.MirrorCS"),sQuery(id+"F7.wireOp",EDGE,"E111.MirrorCS"),sQuery(id+"F7.wireOp",EDGE,"E112.MirrorCS"),sQuery(id+"F7.wireOp",EDGE,"E114.MirrorCS"),sQuery(id+"F7.wireOp",EDGE,"E116.MirrorCS"),sQuery(id+"F7.wireOp",EDGE,"E117.MirrorCS"),sQuery(id+"F7.wireOp",EDGE,"E118.MirrorCS"),sQuery(id+"F7.wireOp",EDGE,"E119.MirrorCS"),sQuery(id+"F7.wireOp",EDGE,"E122.MirrorCS"),sQuery(id+"F7.wireOp",EDGE,"E123.MirrorCS"),sQuery(id+"F7.wireOp",EDGE,"E125.trimOffspring")])],"isStart":false}),makeQuery(id+"F12.opExtrude","CAP_FACE",FACE,{"disambiguationData":[OSD([sQuery(id+"F11.wireOp",EDGE,"E143"),sQuery(id+"F11.wireOp",EDGE,"E144"),sQuery(id+"F11.wireOp",EDGE,"E145.0"),sQuery(id+"F11.wireOp",EDGE,"E145.1"),sQuery(id+"F11.wireOp",EDGE,"E145.2"),sQuery(id+"F11.wireOp",EDGE,"E145.3"),sQuery(id+"F11.wireOp",EDGE,"E146"),sQuery(id+"F11.wireOp",EDGE,"E147"),sQuery(id+"F11.wireOp",EDGE,"E148"),sQuery(id+"F11.wireOp",EDGE,"E149.MirrorCS"),sQuery(id+"F11.wireOp",EDGE,"E150.trimOffspring")])],"isStart":false})]});
            var sketch = newSketch(context, id + "F23", { "sketchPlane" : qUnion([Q0])});
            skLineSegment(sketch, "E207.bottom", {"start": v(-17, 36.5) * mm, "end": v(17, 36.5) * mm});
            skLineSegment(sketch, "E207.top", {"start": v(-17, 32.75) * mm, "end": v(17, 32.75) * mm});
            skLineSegment(sketch, "E207.left", {"start": v(-17, 36.5) * mm, "end": v(-17, 32.75) * mm});
            skLineSegment(sketch, "E207.right", {"start": v(17, 36.5) * mm, "end": v(17, 32.75) * mm});
            skSolve(sketch);
        }
        {
            var Q0;
            Q0=qSketchRegion(id+"F23",true);
            extrude(context, id + "F24", {"entities" : qUnion([Q0]), "operationType" : NewBodyOperationType.REMOVE, "endBound" : BoundingType.THROUGH_ALL, "depth" : 25 * mm});
        }
        {
            var Q0;
            Q0=makeQuery(id+"F24.boolean.opBoolean","MERGE",FACE,{"derivedFrom":[makeQuery(id+"F12.boolean.opBoolean","MERGE",FACE,{"derivedFrom":[makeQuery(id+"F8.opExtrude","CAP_FACE",FACE,{"disambiguationData":[OSD([sQuery(id+"F7.wireOp",EDGE,"E106.0"),sQuery(id+"F7.wireOp",EDGE,"E106.1"),sQuery(id+"F7.wireOp",EDGE,"E106.2"),sQuery(id+"F7.wireOp",EDGE,"E106.3"),sQuery(id+"F7.wireOp",EDGE,"E115.bottom"),sQuery(id+"F7.wireOp",EDGE,"E115.top"),sQuery(id+"F7.wireOp",EDGE,"E115.left"),sQuery(id+"F7.wireOp",EDGE,"E115.right"),sQuery(id+"F7.wireOp",EDGE,"E120"),sQuery(id+"F7.wireOp",EDGE,"E121"),sQuery(id+"F7.wireOp",EDGE,"E124.trimOffspring")])],"isStart":false}),makeQuery(id+"F8.opExtrude","CAP_FACE",FACE,{"disambiguationData":[OSD([sQuery(id+"F7.wireOp",EDGE,"E107.MirrorCS"),sQuery(id+"F7.wireOp",EDGE,"E111.MirrorCS"),sQuery(id+"F7.wireOp",EDGE,"E112.MirrorCS"),sQuery(id+"F7.wireOp",EDGE,"E114.MirrorCS"),sQuery(id+"F7.wireOp",EDGE,"E116.MirrorCS"),sQuery(id+"F7.wireOp",EDGE,"E117.MirrorCS"),sQuery(id+"F7.wireOp",EDGE,"E118.MirrorCS"),sQuery(id+"F7.wireOp",EDGE,"E119.MirrorCS"),sQuery(id+"F7.wireOp",EDGE,"E122.MirrorCS"),sQuery(id+"F7.wireOp",EDGE,"E123.MirrorCS"),sQuery(id+"F7.wireOp",EDGE,"E125.trimOffspring")])],"isStart":false}),makeQuery(id+"F12.opExtrude","CAP_FACE",FACE,{"disambiguationData":[OSD([sQuery(id+"F11.wireOp",EDGE,"E143"),sQuery(id+"F11.wireOp",EDGE,"E144"),sQuery(id+"F11.wireOp",EDGE,"E145.0"),sQuery(id+"F11.wireOp",EDGE,"E145.1"),sQuery(id+"F11.wireOp",EDGE,"E145.2"),sQuery(id+"F11.wireOp",EDGE,"E145.3"),sQuery(id+"F11.wireOp",EDGE,"E146"),sQuery(id+"F11.wireOp",EDGE,"E147"),sQuery(id+"F11.wireOp",EDGE,"E148"),sQuery(id+"F11.wireOp",EDGE,"E149.MirrorCS"),sQuery(id+"F11.wireOp",EDGE,"E150.trimOffspring")])],"isStart":false})]}),makeQuery(id+"F24.opExtrude","CAP_FACE",FACE,{"disambiguationData":[OSD([sQuery(id+"F23.wireOp",EDGE,"E207.bottom"),sQuery(id+"F23.wireOp",EDGE,"E207.top"),sQuery(id+"F23.wireOp",EDGE,"E207.left"),sQuery(id+"F23.wireOp",EDGE,"E207.right")])],"isStart":true})]});
            var sketch = newSketch(context, id + "F25", { "sketchPlane" : qUnion([Q0])});
            skArc(sketch, "E208", {"start": v(12.23, 32.75) * mm, "mid": v(0, 44.98) * mm, "end": v(-12.22, 32.75) * mm});
            skArc(sketch, "E209", {"start": v(23.79, 35.95) * mm, "mid": v(22.17, 41.93) * mm, "end": v(19.08, 47.3) * mm});
            skLineSegment(sketch, "E210", {"start": v(12.23, 32.75) * mm, "end": v(24, 32.75) * mm});
            skLineSegment(sketch, "E211", {"start": v(-24, 32.75) * mm, "end": v(-12.22, 32.75) * mm});
            skCircle(sketch, "E212.cCircle", {"center": v(0, 56.57) * mm, "radius": 2.53 * mm, "construction": true});
            skLineSegment(sketch, "E212.0", {"start": v(1.46, 54.05) * mm, "end": v(-1.46, 54.05) * mm});
            skLineSegment(sketch, "E212.1", {"start": v(-1.46, 54.05) * mm, "end": v(-2.92, 56.57) * mm});
            skLineSegment(sketch, "E212.2", {"start": v(-2.92, 56.57) * mm, "end": v(-1.46, 59.1) * mm, "construction": true});
            skLineSegment(sketch, "E212.3", {"start": v(-1.46, 59.1) * mm, "end": v(1.46, 59.1) * mm, "construction": true});
            skLineSegment(sketch, "E212.4", {"start": v(1.46, 59.1) * mm, "end": v(2.92, 56.57) * mm, "construction": true});
            skLineSegment(sketch, "E212.5", {"start": v(2.92, 56.57) * mm, "end": v(1.46, 54.05) * mm});
            skPoint(sketch, "E212.0.midPoint", {"position": v(0, 54.05) * mm});
            skArc(sketch, "E213.trimOffspring", {"start": v(-2.92, 56.57) * mm, "mid": v(-9.05, 54.98) * mm, "end": v(-14.56, 51.83) * mm});
            skCircle(sketch, "E214.cCircle", {"center": v(-16.82, 49.57) * mm, "radius": 2.77 * mm, "construction": true});
            skLineSegment(sketch, "E214.0", {"start": v(-19.9, 50.4) * mm, "end": v(-17.65, 52.66) * mm, "construction": true});
            skLineSegment(sketch, "E214.1", {"start": v(-17.65, 52.66) * mm, "end": v(-14.56, 51.83) * mm, "construction": true});
            skLineSegment(sketch, "E214.2", {"start": v(-14.56, 51.83) * mm, "end": v(-13.73, 48.74) * mm});
            skLineSegment(sketch, "E214.3", {"start": v(-13.73, 48.74) * mm, "end": v(-16, 46.48) * mm});
            skLineSegment(sketch, "E214.4", {"start": v(-16, 46.48) * mm, "end": v(-19.08, 47.3) * mm});
            skLineSegment(sketch, "E214.5", {"start": v(-19.08, 47.3) * mm, "end": v(-19.9, 50.4) * mm, "construction": true});
            skPoint(sketch, "E214.0.midPoint", {"position": v(-18.78, 51.53) * mm});
            skCircle(sketch, "E215.cCircle", {"center": v(-23.9, 32.75) * mm, "radius": 2.77 * mm, "construction": true});
            skLineSegment(sketch, "E215.0", {"start": v(-26.72, 31.24) * mm, "end": v(-26.6, 34.44) * mm, "construction": true});
            skLineSegment(sketch, "E215.1", {"start": v(-26.6, 34.44) * mm, "end": v(-23.79, 35.95) * mm, "construction": true});
            skLineSegment(sketch, "E215.2", {"start": v(-23.79, 35.95) * mm, "end": v(-21.07, 34.26) * mm});
            skLineSegment(sketch, "E215.3", {"start": v(-21.07, 34.26) * mm, "end": v(-21.12, 32.75) * mm});
            skLineSegment(sketch, "E215.4", {"start": v(-21.18, 31.06) * mm, "end": v(-24, 29.55) * mm, "construction": true});
            skLineSegment(sketch, "E215.5", {"start": v(-24, 29.55) * mm, "end": v(-26.72, 31.24) * mm, "construction": true});
            skPoint(sketch, "E215.0.midPoint", {"position": v(-26.66, 32.84) * mm});
            skLineSegment(sketch, "E216", {"start": v(0, 32.75) * mm, "end": v(-16.82, 49.57) * mm, "construction": true});
            skLineSegment(sketch, "E217", {"start": v(-23.9, 32.75) * mm, "end": v(-24, 32.75) * mm});
            skLineSegment(sketch, "E218.MirrorCS", {"start": v(14.56, 51.83) * mm, "end": v(13.73, 48.74) * mm});
            skLineSegment(sketch, "E219.MirrorCS", {"start": v(13.73, 48.74) * mm, "end": v(16, 46.48) * mm});
            skLineSegment(sketch, "E220.MirrorCS", {"start": v(16, 46.48) * mm, "end": v(19.08, 47.3) * mm});
            skLineSegment(sketch, "E221.MirrorCS", {"start": v(23.79, 35.95) * mm, "end": v(21.07, 34.26) * mm});
            skLineSegment(sketch, "E222.MirrorCS", {"start": v(21.07, 34.26) * mm, "end": v(21.12, 32.75) * mm});
            skArc(sketch, "E223.trimOffspring", {"start": v(14.56, 51.83) * mm, "mid": v(9.05, 54.98) * mm, "end": v(2.92, 56.57) * mm});
            skPoint(sketch, "E224.MirrorCS.end.orphan", {"position": v(24, 32.75) * mm});
            skPoint(sketch, "E224.MirrorCS.start.orphan", {"position": v(21.12, 32.75) * mm});
            skPoint(sketch, "E225.orphan", {"position": v(-21.12, 32.75) * mm});
            skArc(sketch, "E226.trimOffspring", {"start": v(-19.08, 47.3) * mm, "mid": v(-22.17, 41.93) * mm, "end": v(-23.79, 35.95) * mm});
            skSolve(sketch);
        }
        {
            var Q0;
            Q0=qSketchRegion(id+"F25",true);
            extrude(context, id + "F26", {"entities" : qUnion([Q0]), "operationType" : NewBodyOperationType.ADD, "depth" : 99 * mm});
        }
        {
            var Q0;
            {var subQ0=sQuery(id+"F25.wireOp",EDGE,"E208");var subQ1=sQuery(id+"F25.wireOp",EDGE,"E210");Q0=makeQuery(id+"F26.boolean.opBoolean","SPLIT",EDGE,{"disambiguationData":[topologyDisambiguationEdgeConnected([makeQuery(id+"F26.opExtrude","SWEPT_FACE",FACE,{"disambiguationData":[OSD([subQ0])]}),makeQuery(id+"F26.opExtrude","SWEPT_FACE",FACE,{"disambiguationData":[OSD([subQ1])]})])],"derivedFrom":makeQuery(id+"F26.opExtrude","SWEPT_EDGE",EDGE,{"disambiguationData":[OSD([sQuery(id+"F17.wireOp",EDGE,"E171.MirrorCS"),sQuery(id+"F23.wireOp",EDGE,"E207.top"),subQ0,subQ1])]})});}
            var Q1;
            {var subQ0=sQuery(id+"F25.wireOp",EDGE,"E208");var subQ1=makeQuery(id+"F26.opExtrude","SWEPT_FACE",FACE,{"disambiguationData":[OSD([subQ0])]});var subQ2=sQuery(id+"F25.wireOp",EDGE,"E211");var subQ3=makeQuery(id+"F26.opExtrude","SWEPT_FACE",FACE,{"disambiguationData":[OSD([subQ2])]});Q1=makeQuery(id+"F26.boolean.opBoolean","SPLIT",EDGE,{"disambiguationData":[topologyDisambiguationEdgeConnected([subQ1,subQ3]),TD([makeQuery(id+"F1.opExtrude","SWEPT_FACE",FACE,{"disambiguationData":[OSD([sQuery(id+"F0.wireOp",EDGE,"E42")])]})])],"derivedFrom":makeQuery(id+"F26.opExtrude","SWEPT_EDGE",EDGE,{"disambiguationData":[OSD([sQuery(id+"F17.wireOp",EDGE,"E166"),sQuery(id+"F23.wireOp",EDGE,"E207.top"),subQ0,subQ2])]})});}
            var Q2;
            {var subQ0=sQuery(id+"F25.wireOp",EDGE,"E211");var subQ1=makeQuery(id+"F26.opExtrude","SWEPT_FACE",FACE,{"disambiguationData":[OSD([subQ0])]});var subQ2=sQuery(id+"F25.wireOp",EDGE,"E208");var subQ3=makeQuery(id+"F26.opExtrude","SWEPT_FACE",FACE,{"disambiguationData":[OSD([subQ2])]});Q2=makeQuery(id+"F26.boolean.opBoolean","SPLIT",EDGE,{"disambiguationData":[topologyDisambiguationEdgeConnected([subQ3,subQ1]),TD([makeQuery(id+"F1.opExtrude","SWEPT_FACE",FACE,{"disambiguationData":[OSD([sQuery(id+"F0.wireOp",EDGE,"E45.MirrorCS")])]})])],"derivedFrom":makeQuery(id+"F26.opExtrude","SWEPT_EDGE",EDGE,{"disambiguationData":[OSD([sQuery(id+"F17.wireOp",EDGE,"E166"),sQuery(id+"F23.wireOp",EDGE,"E207.top"),subQ2,subQ0])]})});}
            chamfer(context, id + "F27", {"entities" : qUnion([Q0, Q1, Q2]), "width" : 5 * mm, "tangentPropagation" : true});
        }
        {
            var Q0;
            Q0=makeQuery(id+"F26.opExtrude","CAP_EDGE",EDGE,{"disambiguationData":[OSD([sQuery(id+"F25.wireOp",EDGE,"E208")])],"isStart":true});
            chamfer(context, id + "F28", {"entities" : qUnion([Q0]), "width" : 1.6 * mm, "tangentPropagation" : true});
        }
        {
            var Q0;
            Q0=makeQuery(id+"F1.opExtrude","SWEPT_FACE",FACE,{"disambiguationData":[OSD([sQuery(id+"F0.wireOp",EDGE,"E39.MirrorCS")])]});
            var sketch = newSketch(context, id + "F29", { "sketchPlane" : qUnion([Q0])});
            skCircle(sketch, "E227", {"center": v(0, 32.75) * mm, "radius": 12.23 * mm});
            skCircle(sketch, "E228", {"center": v(0, 32.75) * mm, "radius": 4 * mm});
            skSolve(sketch);
        }
        {
            var Q0;
            Q0=qSketchRegion(id+"F29",true);
            extrude(context, id + "F30", {"entities" : qUnion([Q0]), "operationType" : NewBodyOperationType.ADD, "oppositeDirection" : true, "depth" : 10 * mm});
        }
        {
            var Q0;
            {var subQ0=sQuery(id+"F29.wireOp",EDGE,"E227");Q0=makeQuery(id+"F30.boolean.opBoolean","SPLIT",EDGE,{"disambiguationData":[topologyDisambiguationEdgeConnected([makeQuery(id+"F30.opExtrude","SWEPT_FACE",FACE,{"disambiguationData":[OSD([subQ0])]})])],"derivedFrom":makeQuery(id+"F30.opExtrude","CAP_EDGE",EDGE,{"disambiguationData":[OSD([subQ0])],"isStart":true})});}
            chamfer(context, id + "F31", {"entities" : qUnion([Q0]), "width" : 5 * mm, "tangentPropagation" : true});
        }
        {
            var Q0;
            {var subQ1=makeQuery(id+"F1.opExtrude","SWEPT_FACE",FACE,{"disambiguationData":[OSD([sQuery(id+"F0.wireOp",EDGE,"E27.MirrorCS")])]});var subQ2=sQuery(id+"F29.wireOp",EDGE,"E227");var subQ4=makeQuery(id+"F30.opExtrude","SWEPT_FACE",FACE,{"disambiguationData":[OSD([subQ2])]});Q0=makeQuery(id+"F31.opChamfer","BLEND_EDGE",EDGE,{"blendedFrom":[makeQuery(id+"F30.boolean.opBoolean","SPLIT",EDGE,{"disambiguationData":[topologyDisambiguationEdgeConnected([subQ4])],"derivedFrom":makeQuery(id+"F30.opExtrude","CAP_EDGE",EDGE,{"disambiguationData":[OSD([subQ2])],"isStart":true})}),makeQuery(id+"F30.boolean.opBoolean","SPLIT",FACE,{"disambiguationData":[TD([subQ1])],"derivedFrom":subQ4})],"blendedInto":[makeQuery(id+"F30.boolean.opBoolean","SPLIT",FACE,{"disambiguationData":[TD([subQ1])],"derivedFrom":subQ4})]});}
            chamfer(context, id + "F32", {"entities" : qUnion([Q0]), "width" : 5 * mm, "tangentPropagation" : true});
        }
        {
            var Q0;
            Q0=makeQuery(id+"F5n87RI4xKnIYEv_2.boolean.opBoolean","MERGE",FACE,{"derivedFrom":[makeQuery(id+"F18.opExtrude","SWEPT_FACE",FACE,{"disambiguationData":[OSD([sQuery(id+"F17.wireOp",EDGE,"E197")])]}),makeQuery(id+"F5n87RI4xKnIYEv_2.opExtrude","CAP_FACE",FACE,{"disambiguationData":[OSD([sQuery(id+"F6pmPqNWny6qC9j_2.wireOp",EDGE,"pMz0czM6-3MVS-HfZV-ye4E-MwDP2wHDbyg5"),sQuery(id+"F6pmPqNWny6qC9j_2.wireOp",EDGE,"mWCL9m8I-v7ZP-wYf1-pQOj-59Lfgnsu26d9"),sQuery(id+"F6pmPqNWny6qC9j_2.wireOp",EDGE,"wS4K9Q2B-4UkM-grFq-TAIq-GnapL3y45tF9"),sQuery(id+"F6pmPqNWny6qC9j_2.wireOp",EDGE,"dAXueDyM-mQtb-UpcX-YQIT-BihZSuAXyMLI")])],"isStart":true})]});
            var sketch = newSketch(context, id + "F33", { "sketchPlane" : qUnion([Q0])});
            skCircle(sketch, "E229", {"center": v(0, 32.75) * mm, "radius": 25 * mm});
            skSolve(sketch);
        }
        {
            var Q0;
            Q0=qSketchRegion(id+"F33",true);
            extrude(context, id + "F34", {"entities" : qUnion([Q0]), "operationType" : NewBodyOperationType.REMOVE, "depth" : 25 * mm});
        }
        {
            var Q0;
            Q0=qCreatedBy(makeId("Top.planeOp"),FACE);
            var sketch = newSketch(context, id + "F35", { "sketchPlane" : qUnion([Q0])});
            skCircle(sketch, "E230.cCircle", {"center": v(-30, 24) * mm, "radius": 5.54 * mm, "construction": true});
            skLineSegment(sketch, "E230.0", {"start": v(-33.2, 29.54) * mm, "end": v(-26.8, 29.54) * mm});
            skLineSegment(sketch, "E230.1", {"start": v(-26.8, 29.54) * mm, "end": v(-23.6, 24) * mm});
            skLineSegment(sketch, "E230.2", {"start": v(-23.6, 24) * mm, "end": v(-26.8, 18.46) * mm});
            skLineSegment(sketch, "E230.3", {"start": v(-26.8, 18.46) * mm, "end": v(-33.2, 18.46) * mm});
            skLineSegment(sketch, "E230.4", {"start": v(-33.2, 18.46) * mm, "end": v(-36.4, 24) * mm});
            skLineSegment(sketch, "E230.5", {"start": v(-36.4, 24) * mm, "end": v(-33.2, 29.54) * mm});
            skPoint(sketch, "E230.0.midPoint", {"position": v(-30, 29.54) * mm});
            skLineSegment(sketch, "E231.MirrorCS", {"start": v(26.8, 29.54) * mm, "end": v(23.6, 24) * mm});
            skCircle(sketch, "E232.MirrorC", {"center": v(30, 24) * mm, "radius": 5.54 * mm, "construction": true});
            skLineSegment(sketch, "E233.MirrorCS", {"start": v(33.2, 18.46) * mm, "end": v(36.4, 24) * mm});
            skPoint(sketch, "E234.MirrorP", {"position": v(30, 29.54) * mm});
            skLineSegment(sketch, "E235.MirrorCS", {"start": v(36.4, 24) * mm, "end": v(33.2, 29.54) * mm});
            skLineSegment(sketch, "E236.MirrorCS", {"start": v(26.8, 18.46) * mm, "end": v(33.2, 18.46) * mm});
            skLineSegment(sketch, "E237.MirrorCS", {"start": v(33.2, 29.54) * mm, "end": v(26.8, 29.54) * mm});
            skLineSegment(sketch, "E238.MirrorCS", {"start": v(23.6, 24) * mm, "end": v(26.8, 18.46) * mm});
            skLineSegment(sketch, "E239.MirrorCS", {"start": v(36.4, -24) * mm, "end": v(33.2, -29.54) * mm});
            skLineSegment(sketch, "E240.MirrorCS", {"start": v(-26.8, -29.54) * mm, "end": v(-23.6, -24) * mm});
            skLineSegment(sketch, "E241.MirrorCS", {"start": v(-33.2, -29.54) * mm, "end": v(-26.8, -29.54) * mm});
            skLineSegment(sketch, "E242.MirrorCS", {"start": v(-23.6, -24) * mm, "end": v(-26.8, -18.46) * mm});
            skLineSegment(sketch, "E243.MirrorCS", {"start": v(23.6, -24) * mm, "end": v(26.8, -18.46) * mm});
            skLineSegment(sketch, "E244.MirrorCS", {"start": v(26.8, -18.46) * mm, "end": v(33.2, -18.46) * mm});
            skPoint(sketch, "E245.MirrorP", {"position": v(30, -29.54) * mm});
            skPoint(sketch, "E246.MirrorP", {"position": v(-30, -29.54) * mm});
            skLineSegment(sketch, "E247.MirrorCS", {"start": v(33.2, -29.54) * mm, "end": v(26.8, -29.54) * mm});
            skCircle(sketch, "E248.MirrorC", {"center": v(30, -24) * mm, "radius": 5.54 * mm, "construction": true});
            skCircle(sketch, "E249.MirrorC", {"center": v(-30, -24) * mm, "radius": 5.54 * mm, "construction": true});
            skLineSegment(sketch, "E250.MirrorCS", {"start": v(33.2, -18.46) * mm, "end": v(36.4, -24) * mm});
            skLineSegment(sketch, "E251.MirrorCS", {"start": v(-36.4, -24) * mm, "end": v(-33.2, -29.54) * mm});
            skLineSegment(sketch, "E252.MirrorCS", {"start": v(-26.8, -18.46) * mm, "end": v(-33.2, -18.46) * mm});
            skLineSegment(sketch, "E253.MirrorCS", {"start": v(26.8, -29.54) * mm, "end": v(23.6, -24) * mm});
            skLineSegment(sketch, "E254.MirrorCS", {"start": v(-33.2, -18.46) * mm, "end": v(-36.4, -24) * mm});
            skSolve(sketch);
        }
        {
            var Q0;
            Q0=qSketchRegion(id+"F35",true);
            extrude(context, id + "F36", {"entities" : qUnion([Q0]), "operationType" : NewBodyOperationType.REMOVE, "endBound" : BoundingType.THROUGH_ALL, "depth" : 25 * mm});
        }
        {
            var Q0;
            {var subQ0=sQuery(id+"F25.wireOp",EDGE,"E226.trimOffspring");var subQ1=sQuery(id+"F25.wireOp",EDGE,"E215.2");var subQ2=sQuery(id+"F11.wireOp",EDGE,"E144");Q0=makeQuery(id+"F36.boolean.opBoolean","SPLIT",EDGE,{"disambiguationData":[TD([makeQuery(id+"F36.opExtrude","SWEPT_FACE",FACE,{"disambiguationData":[OSD([sQuery(id+"F35.wireOp",EDGE,"E242.MirrorCS")])]})])],"derivedFrom":makeQuery(id+"F26.opExtrude","SWEPT_EDGE",EDGE,{"disambiguationData":[OSD([subQ2,subQ1,subQ0])]})});}
            var Q1;
            {var subQ0=sQuery(id+"F25.wireOp",EDGE,"E226.trimOffspring");var subQ1=sQuery(id+"F25.wireOp",EDGE,"E215.2");var subQ3=sQuery(id+"F11.wireOp",EDGE,"E144");Q1=makeQuery(id+"F36.boolean.opBoolean","SPLIT",EDGE,{"disambiguationData":[TD([makeQuery(id+"F36.opExtrude","SWEPT_FACE",FACE,{"disambiguationData":[OSD([sQuery(id+"F35.wireOp",EDGE,"E250.MirrorCS")])]})])],"derivedFrom":makeQuery(id+"F26.opExtrude","SWEPT_EDGE",EDGE,{"disambiguationData":[OSD([subQ3,subQ1,subQ0])]})});}
            var Q2;
            {var subQ0=sQuery(id+"F25.wireOp",EDGE,"E215.2");var subQ2=sQuery(id+"F11.wireOp",EDGE,"E144");var subQ3=sQuery(id+"F25.wireOp",EDGE,"E226.trimOffspring");Q2=makeQuery(id+"F36.boolean.opBoolean","SPLIT",EDGE,{"disambiguationData":[TD([makeQuery(id+"F36.opExtrude","SWEPT_FACE",FACE,{"disambiguationData":[OSD([sQuery(id+"F35.wireOp",EDGE,"E254.MirrorCS")])]})])],"derivedFrom":makeQuery(id+"F26.opExtrude","SWEPT_EDGE",EDGE,{"disambiguationData":[OSD([subQ2,subQ0,subQ3])]})});}
            var Q3;
            Q3=makeQuery(id+"F26.opExtrude","SWEPT_EDGE",EDGE,{"disambiguationData":[OSD([sQuery(id+"F11.wireOp",EDGE,"E144"),sQuery(id+"F25.wireOp",EDGE,"E213.trimOffspring"),sQuery(id+"F25.wireOp",EDGE,"E214.2")])]});
            var Q4;
            Q4=makeQuery(id+"F26.opExtrude","SWEPT_EDGE",EDGE,{"disambiguationData":[OSD([sQuery(id+"F11.wireOp",EDGE,"E150.trimOffspring"),sQuery(id+"F25.wireOp",EDGE,"E218.MirrorCS"),sQuery(id+"F25.wireOp",EDGE,"E223.trimOffspring")])]});
            var Q5;
            {var subQ0=sQuery(id+"F25.wireOp",EDGE,"E221.MirrorCS");var subQ1=sQuery(id+"F11.wireOp",EDGE,"E150.trimOffspring");var subQ2=sQuery(id+"F25.wireOp",EDGE,"E209");Q5=makeQuery(id+"F36.boolean.opBoolean","SPLIT",EDGE,{"disambiguationData":[TD([makeQuery(id+"F36.opExtrude","SWEPT_FACE",FACE,{"disambiguationData":[OSD([sQuery(id+"F35.wireOp",EDGE,"E230.2")])]})])],"derivedFrom":makeQuery(id+"F26.opExtrude","SWEPT_EDGE",EDGE,{"disambiguationData":[OSD([subQ1,subQ2,subQ0])]})});}
            var Q6;
            {var subQ1=sQuery(id+"F25.wireOp",EDGE,"E221.MirrorCS");var subQ2=sQuery(id+"F11.wireOp",EDGE,"E150.trimOffspring");var subQ3=sQuery(id+"F25.wireOp",EDGE,"E209");Q6=makeQuery(id+"F36.boolean.opBoolean","SPLIT",EDGE,{"disambiguationData":[TD([makeQuery(id+"F36.opExtrude","SWEPT_FACE",FACE,{"disambiguationData":[OSD([sQuery(id+"F35.wireOp",EDGE,"E233.MirrorCS")])]})])],"derivedFrom":makeQuery(id+"F26.opExtrude","SWEPT_EDGE",EDGE,{"disambiguationData":[OSD([subQ2,subQ3,subQ1])]})});}
            var Q7;
            {var subQ0=sQuery(id+"F25.wireOp",EDGE,"E209");var subQ1=sQuery(id+"F11.wireOp",EDGE,"E150.trimOffspring");var subQ3=sQuery(id+"F25.wireOp",EDGE,"E221.MirrorCS");Q7=makeQuery(id+"F36.boolean.opBoolean","SPLIT",EDGE,{"disambiguationData":[TD([makeQuery(id+"F36.opExtrude","SWEPT_FACE",FACE,{"disambiguationData":[OSD([sQuery(id+"F35.wireOp",EDGE,"E230.4")])]})])],"derivedFrom":makeQuery(id+"F26.opExtrude","SWEPT_EDGE",EDGE,{"disambiguationData":[OSD([subQ1,subQ0,subQ3])]})});}
            var Q8;
            {var subQ0=sQuery(id+"F25.wireOp",EDGE,"E226.trimOffspring");var subQ1=sQuery(id+"F25.wireOp",EDGE,"E214.4");var subQ2=sQuery(id+"F11.wireOp",EDGE,"E144");Q8=makeQuery(id+"F36.boolean.opBoolean","SPLIT",EDGE,{"disambiguationData":[TD([makeQuery(id+"F36.opExtrude","SWEPT_FACE",FACE,{"disambiguationData":[OSD([sQuery(id+"F35.wireOp",EDGE,"E242.MirrorCS")])]})])],"derivedFrom":makeQuery(id+"F26.opExtrude","SWEPT_EDGE",EDGE,{"disambiguationData":[OSD([subQ2,subQ1,subQ0])]})});}
            var Q9;
            Q9=makeQuery(id+"F26.opExtrude","SWEPT_EDGE",EDGE,{"disambiguationData":[OSD([sQuery(id+"F11.wireOp",EDGE,"E145.3"),sQuery(id+"F11.wireOp",EDGE,"E148"),sQuery(id+"F25.wireOp",EDGE,"E212.1"),sQuery(id+"F25.wireOp",EDGE,"E213.trimOffspring")])]});
            var Q10;
            Q10=makeQuery(id+"F26.opExtrude","SWEPT_EDGE",EDGE,{"disambiguationData":[OSD([sQuery(id+"F11.wireOp",EDGE,"E145.0"),sQuery(id+"F11.wireOp",EDGE,"E149.MirrorCS"),sQuery(id+"F25.wireOp",EDGE,"E212.5"),sQuery(id+"F25.wireOp",EDGE,"E223.trimOffspring")])]});
            var Q11;
            {var subQ0=sQuery(id+"F25.wireOp",EDGE,"E220.MirrorCS");var subQ1=sQuery(id+"F11.wireOp",EDGE,"E150.trimOffspring");var subQ2=sQuery(id+"F25.wireOp",EDGE,"E209");Q11=makeQuery(id+"F36.boolean.opBoolean","SPLIT",EDGE,{"disambiguationData":[TD([makeQuery(id+"F36.opExtrude","SWEPT_FACE",FACE,{"disambiguationData":[OSD([sQuery(id+"F35.wireOp",EDGE,"E230.2")])]})])],"derivedFrom":makeQuery(id+"F26.opExtrude","SWEPT_EDGE",EDGE,{"disambiguationData":[OSD([subQ1,subQ2,subQ0])]})});}
            var Q12;
            {var subQ0=sQuery(id+"F17.wireOp",EDGE,"E196");var subQ1=sQuery(id+"F17.wireOp",EDGE,"E176");var subQ2=sQuery(id+"F17.wireOp",EDGE,"E167");Q12=makeQuery(id+"F36.boolean.opBoolean","SPLIT",EDGE,{"disambiguationData":[TD([makeQuery(id+"F36.opExtrude","SWEPT_FACE",FACE,{"disambiguationData":[OSD([sQuery(id+"F35.wireOp",EDGE,"E254.MirrorCS")])]})])],"derivedFrom":makeQuery(id+"F5n87RI4xKnIYEv_2.boolean.opBoolean","SPLIT",EDGE,{"derivedFrom":makeQuery(id+"F18.opExtrude","CAP_EDGE",EDGE,{"disambiguationData":[OSD([subQ2,subQ1,subQ0])],"isStart":false})})});}
            var Q13;
            {var subQ0=sQuery(id+"F17.wireOp",EDGE,"E196");var subQ1=sQuery(id+"F17.wireOp",EDGE,"E176");var subQ2=sQuery(id+"F17.wireOp",EDGE,"E167");Q13=makeQuery(id+"F36.boolean.opBoolean","SPLIT",EDGE,{"disambiguationData":[TD([makeQuery(id+"F36.opExtrude","SWEPT_FACE",FACE,{"disambiguationData":[OSD([sQuery(id+"F35.wireOp",EDGE,"E242.MirrorCS")])]})])],"derivedFrom":makeQuery(id+"F5n87RI4xKnIYEv_2.boolean.opBoolean","SPLIT",EDGE,{"derivedFrom":makeQuery(id+"F18.opExtrude","CAP_EDGE",EDGE,{"disambiguationData":[OSD([subQ2,subQ1,subQ0])],"isStart":false})})});}
            var Q14;
            {var subQ0=sQuery(id+"F17.wireOp",EDGE,"E196");var subQ1=sQuery(id+"F17.wireOp",EDGE,"E176");var subQ2=sQuery(id+"F17.wireOp",EDGE,"E167");Q14=makeQuery(id+"F36.boolean.opBoolean","SPLIT",EDGE,{"disambiguationData":[TD([makeQuery(id+"F36.opExtrude","SWEPT_FACE",FACE,{"disambiguationData":[OSD([sQuery(id+"F35.wireOp",EDGE,"E250.MirrorCS")])]})])],"derivedFrom":makeQuery(id+"F5n87RI4xKnIYEv_2.boolean.opBoolean","SPLIT",EDGE,{"derivedFrom":makeQuery(id+"F18.opExtrude","CAP_EDGE",EDGE,{"disambiguationData":[OSD([subQ2,subQ1,subQ0])],"isStart":false})})});}
            var Q15;
            {var subQ0=sQuery(id+"F17.wireOp",EDGE,"E198");var subQ1=sQuery(id+"F17.wireOp",EDGE,"E185");var subQ2=sQuery(id+"F17.wireOp",EDGE,"E173.MirrorCS");Q15=makeQuery(id+"F36.boolean.opBoolean","SPLIT",EDGE,{"disambiguationData":[TD([makeQuery(id+"F36.opExtrude","SWEPT_FACE",FACE,{"disambiguationData":[OSD([sQuery(id+"F35.wireOp",EDGE,"E230.4")])]})])],"derivedFrom":makeQuery(id+"F5n87RI4xKnIYEv_2.boolean.opBoolean","SPLIT",EDGE,{"derivedFrom":makeQuery(id+"F18.opExtrude","CAP_EDGE",EDGE,{"disambiguationData":[OSD([subQ2,subQ1,subQ0])],"isStart":false})})});}
            var Q16;
            {var subQ0=sQuery(id+"F17.wireOp",EDGE,"E198");var subQ1=sQuery(id+"F17.wireOp",EDGE,"E185");var subQ2=sQuery(id+"F17.wireOp",EDGE,"E173.MirrorCS");Q16=makeQuery(id+"F36.boolean.opBoolean","SPLIT",EDGE,{"disambiguationData":[TD([makeQuery(id+"F36.opExtrude","SWEPT_FACE",FACE,{"disambiguationData":[OSD([sQuery(id+"F35.wireOp",EDGE,"E230.2")])]})])],"derivedFrom":makeQuery(id+"F5n87RI4xKnIYEv_2.boolean.opBoolean","SPLIT",EDGE,{"derivedFrom":makeQuery(id+"F18.opExtrude","CAP_EDGE",EDGE,{"disambiguationData":[OSD([subQ2,subQ1,subQ0])],"isStart":false})})});}
            var Q17;
            {var subQ0=sQuery(id+"F17.wireOp",EDGE,"E198");var subQ1=sQuery(id+"F17.wireOp",EDGE,"E185");var subQ2=sQuery(id+"F17.wireOp",EDGE,"E173.MirrorCS");Q17=makeQuery(id+"F36.boolean.opBoolean","SPLIT",EDGE,{"disambiguationData":[TD([makeQuery(id+"F36.opExtrude","SWEPT_FACE",FACE,{"disambiguationData":[OSD([sQuery(id+"F35.wireOp",EDGE,"E233.MirrorCS")])]})])],"derivedFrom":makeQuery(id+"F5n87RI4xKnIYEv_2.boolean.opBoolean","SPLIT",EDGE,{"derivedFrom":makeQuery(id+"F18.opExtrude","CAP_EDGE",EDGE,{"disambiguationData":[OSD([subQ2,subQ1,subQ0])],"isStart":false})})});}
            chamfer(context, id + "F37", {"entities" : qUnion([Q0, Q1, Q2, Q3, Q4, Q5, Q6, Q7, Q8, Q9, Q10, Q11, Q12, Q13, Q14, Q15, Q16, Q17]), "width" : 2.5 * mm, "tangentPropagation" : true});
        }
        {
            var Q0;
            Q0=makeQuery(id+"F26.opExtrude","CAP_EDGE",EDGE,{"disambiguationData":[OSD([sQuery(id+"F25.wireOp",EDGE,"E215.3")])],"isStart":true});
            var Q1;
            Q1=makeQuery(id+"F26.opExtrude","CAP_EDGE",EDGE,{"disambiguationData":[OSD([sQuery(id+"F25.wireOp",EDGE,"E214.3")])],"isStart":true});
            var Q2;
            Q2=makeQuery(id+"F26.opExtrude","CAP_EDGE",EDGE,{"disambiguationData":[OSD([sQuery(id+"F25.wireOp",EDGE,"E222.MirrorCS")])],"isStart":true});
            var Q3;
            Q3=makeQuery(id+"F26.opExtrude","CAP_EDGE",EDGE,{"disambiguationData":[OSD([sQuery(id+"F25.wireOp",EDGE,"E219.MirrorCS")])],"isStart":true});
            chamfer(context, id + "F38", {"entities" : qUnion([Q0, Q1, Q2, Q3]), "width" : 5 * mm, "tangentPropagation" : true});
        }
        {
            var Q0;
            Q0=qCreatedBy(makeId("Top.planeOp"),FACE);
            var sketch = newSketch(context, id + "F39", { "sketchPlane" : qUnion([Q0])});
            skLineSegment(sketch, "E255", {"start": v(0, -24) * mm, "end": v(-17.2, -24) * mm});
            skLineSegment(sketch, "E256", {"start": v(-17.2, -24) * mm, "end": v(-14.31, -19) * mm});
            skLineSegment(sketch, "E257", {"start": v(-14.31, -19) * mm, "end": v(0, -19) * mm});
            skLineSegment(sketch, "E258.MirrorCS", {"start": v(14.31, -19) * mm, "end": v(0, -19) * mm});
            skLineSegment(sketch, "E259.MirrorCS", {"start": v(17.2, -24) * mm, "end": v(14.31, -19) * mm});
            skLineSegment(sketch, "E260.MirrorCS", {"start": v(0, -24) * mm, "end": v(17.2, -24) * mm});
            skLineSegment(sketch, "E261.MirrorCS", {"start": v(0, 24) * mm, "end": v(17.2, 24) * mm});
            skLineSegment(sketch, "E262.MirrorCS", {"start": v(14.31, 19) * mm, "end": v(0, 19) * mm});
            skLineSegment(sketch, "E263.MirrorCS", {"start": v(-17.2, 24) * mm, "end": v(-14.31, 19) * mm});
            skLineSegment(sketch, "E264.MirrorCS", {"start": v(-14.31, 19) * mm, "end": v(0, 19) * mm});
            skLineSegment(sketch, "E265.MirrorCS", {"start": v(0, 24) * mm, "end": v(-17.2, 24) * mm});
            skLineSegment(sketch, "E266.MirrorCS", {"start": v(17.2, 24) * mm, "end": v(14.31, 19) * mm});
            skSolve(sketch);
        }
        {
            var Q0;
            Q0=qSketchRegion(id+"F39",true);
            extrude(context, id + "F40", {"entities" : qUnion([Q0]), "operationType" : NewBodyOperationType.REMOVE, "endBound" : BoundingType.THROUGH_ALL, "depth" : 25 * mm});
        }
        {
            var Q0;
            Q0=makeQuery(id+"F40.boolean.opBoolean","INTERSECT",EDGE,{"derivedFrom":[makeQuery(id+"F37.opChamfer","BLEND_FACE",FACE,{"disambiguationData":[OSD([sQuery(id+"F11.wireOp",EDGE,"E144"),sQuery(id+"F25.wireOp",EDGE,"E214.4"),sQuery(id+"F25.wireOp",EDGE,"E226.trimOffspring")])]}),makeQuery(id+"F40.opExtrude","SWEPT_FACE",FACE,{"disambiguationData":[OSD([sQuery(id+"F39.wireOp",EDGE,"E257"),sQuery(id+"F39.wireOp",EDGE,"E258.MirrorCS")])]})]});
            var Q1;
            {var subQ0=sQuery(id+"F25.wireOp",EDGE,"E226.trimOffspring");var subQ1=sQuery(id+"F25.wireOp",EDGE,"E214.4");var subQ2=sQuery(id+"F11.wireOp",EDGE,"E144");Q1=makeQuery(id+"F37.opChamfer","BLEND_EDGE",EDGE,{"blendedFrom":[makeQuery(id+"F36.boolean.opBoolean","SPLIT",EDGE,{"disambiguationData":[TD([makeQuery(id+"F36.opExtrude","SWEPT_FACE",FACE,{"disambiguationData":[OSD([sQuery(id+"F35.wireOp",EDGE,"E242.MirrorCS")])]})])],"derivedFrom":makeQuery(id+"F26.opExtrude","SWEPT_EDGE",EDGE,{"disambiguationData":[OSD([subQ2,subQ1,subQ0])]})}),makeQuery(id+"F36.boolean.opBoolean","COPY",FACE,{"derivedFrom":makeQuery(id+"F36.opExtrude","SWEPT_FACE",FACE,{"disambiguationData":[OSD([sQuery(id+"F35.wireOp",EDGE,"E244.MirrorCS")])]})})],"blendedInto":[makeQuery(id+"F36.boolean.opBoolean","COPY",FACE,{"derivedFrom":makeQuery(id+"F36.opExtrude","SWEPT_FACE",FACE,{"disambiguationData":[OSD([sQuery(id+"F35.wireOp",EDGE,"E244.MirrorCS")])]})})]});}
            var Q2;
            {var subQ0=sQuery(id+"F25.wireOp",EDGE,"E226.trimOffspring");var subQ1=sQuery(id+"F25.wireOp",EDGE,"E214.4");var subQ2=sQuery(id+"F11.wireOp",EDGE,"E144");Q2=makeQuery(id+"F37.opChamfer","BLEND_EDGE",EDGE,{"blendedFrom":[makeQuery(id+"F36.boolean.opBoolean","SPLIT",EDGE,{"disambiguationData":[TD([makeQuery(id+"F36.opExtrude","SWEPT_FACE",FACE,{"disambiguationData":[OSD([sQuery(id+"F35.wireOp",EDGE,"E242.MirrorCS")])]})])],"derivedFrom":makeQuery(id+"F26.opExtrude","SWEPT_EDGE",EDGE,{"disambiguationData":[OSD([subQ2,subQ1,subQ0])]})}),makeQuery(id+"F36.boolean.opBoolean","COPY",FACE,{"derivedFrom":makeQuery(id+"F36.opExtrude","SWEPT_FACE",FACE,{"disambiguationData":[OSD([sQuery(id+"F35.wireOp",EDGE,"E252.MirrorCS")])]})})],"blendedInto":[makeQuery(id+"F36.boolean.opBoolean","COPY",FACE,{"derivedFrom":makeQuery(id+"F36.opExtrude","SWEPT_FACE",FACE,{"disambiguationData":[OSD([sQuery(id+"F35.wireOp",EDGE,"E252.MirrorCS")])]})})]});}
            var Q3;
            Q3=makeQuery(id+"F40.boolean.opBoolean","INTERSECT",EDGE,{"derivedFrom":[makeQuery(id+"F37.opChamfer","BLEND_FACE",FACE,{"disambiguationData":[OSD([sQuery(id+"F11.wireOp",EDGE,"E150.trimOffspring"),sQuery(id+"F25.wireOp",EDGE,"E209"),sQuery(id+"F25.wireOp",EDGE,"E220.MirrorCS")])]}),makeQuery(id+"F40.opExtrude","SWEPT_FACE",FACE,{"disambiguationData":[OSD([sQuery(id+"F39.wireOp",EDGE,"E262.MirrorCS"),sQuery(id+"F39.wireOp",EDGE,"E264.MirrorCS")])]})]});
            var Q4;
            {var subQ0=sQuery(id+"F25.wireOp",EDGE,"E220.MirrorCS");var subQ1=sQuery(id+"F11.wireOp",EDGE,"E150.trimOffspring");var subQ2=sQuery(id+"F25.wireOp",EDGE,"E209");Q4=makeQuery(id+"F37.opChamfer","BLEND_EDGE",EDGE,{"blendedFrom":[makeQuery(id+"F36.boolean.opBoolean","SPLIT",EDGE,{"disambiguationData":[TD([makeQuery(id+"F36.opExtrude","SWEPT_FACE",FACE,{"disambiguationData":[OSD([sQuery(id+"F35.wireOp",EDGE,"E230.2")])]})])],"derivedFrom":makeQuery(id+"F26.opExtrude","SWEPT_EDGE",EDGE,{"disambiguationData":[OSD([subQ1,subQ2,subQ0])]})}),makeQuery(id+"F36.boolean.opBoolean","COPY",FACE,{"derivedFrom":makeQuery(id+"F36.opExtrude","SWEPT_FACE",FACE,{"disambiguationData":[OSD([sQuery(id+"F35.wireOp",EDGE,"E236.MirrorCS")])]})})],"blendedInto":[makeQuery(id+"F36.boolean.opBoolean","COPY",FACE,{"derivedFrom":makeQuery(id+"F36.opExtrude","SWEPT_FACE",FACE,{"disambiguationData":[OSD([sQuery(id+"F35.wireOp",EDGE,"E236.MirrorCS")])]})})]});}
            var Q5;
            {var subQ0=sQuery(id+"F25.wireOp",EDGE,"E220.MirrorCS");var subQ1=sQuery(id+"F11.wireOp",EDGE,"E150.trimOffspring");var subQ2=sQuery(id+"F25.wireOp",EDGE,"E209");Q5=makeQuery(id+"F37.opChamfer","BLEND_EDGE",EDGE,{"blendedFrom":[makeQuery(id+"F36.boolean.opBoolean","SPLIT",EDGE,{"disambiguationData":[TD([makeQuery(id+"F36.opExtrude","SWEPT_FACE",FACE,{"disambiguationData":[OSD([sQuery(id+"F35.wireOp",EDGE,"E230.2")])]})])],"derivedFrom":makeQuery(id+"F26.opExtrude","SWEPT_EDGE",EDGE,{"disambiguationData":[OSD([subQ1,subQ2,subQ0])]})}),makeQuery(id+"F36.boolean.opBoolean","COPY",FACE,{"derivedFrom":makeQuery(id+"F36.opExtrude","SWEPT_FACE",FACE,{"disambiguationData":[OSD([sQuery(id+"F35.wireOp",EDGE,"E230.3")])]})})],"blendedInto":[makeQuery(id+"F36.boolean.opBoolean","COPY",FACE,{"derivedFrom":makeQuery(id+"F36.opExtrude","SWEPT_FACE",FACE,{"disambiguationData":[OSD([sQuery(id+"F35.wireOp",EDGE,"E230.3")])]})})]});}
            chamfer(context, id + "F41", {"entities" : qUnion([Q0, Q1, Q2, Q3, Q4, Q5]), "width" : 1.5 * mm, "tangentPropagation" : true});
        }
        {
            var Q0;
            Q0=qCreatedBy(makeId("Right.planeOp"),FACE);
            cPlane(context, id + "F42", {"entities" : qUnion([Q0]), "cplaneType" : CPlaneType.OFFSET, "offset" : 47 * mm, "width" : 150 * mm, "height" : 150 * mm});
        }
        {
            var Q0;
            Q0=qCreatedBy(id+"F42.planeOp",FACE);
            var sketch = newSketch(context, id + "F43", { "sketchPlane" : qUnion([Q0])});
            skCircle(sketch, "E267.cCircle", {"center": v(0, 46) * mm, "radius": 2.92 * mm, "construction": true});
            skLineSegment(sketch, "E267.0", {"start": v(2.92, 47.68) * mm, "end": v(2.92, 44.32) * mm});
            skLineSegment(sketch, "E267.1", {"start": v(2.92, 44.32) * mm, "end": v(0, 42.63) * mm});
            skLineSegment(sketch, "E267.2", {"start": v(0, 42.63) * mm, "end": v(-2.92, 44.32) * mm});
            skLineSegment(sketch, "E267.3", {"start": v(-2.92, 44.32) * mm, "end": v(-2.92, 47.68) * mm});
            skLineSegment(sketch, "E267.4", {"start": v(-2.92, 47.68) * mm, "end": v(0, 49.37) * mm, "construction": true});
            skLineSegment(sketch, "E267.5", {"start": v(0, 49.37) * mm, "end": v(2.92, 47.68) * mm, "construction": true});
            skPoint(sketch, "E267.0.midPoint", {"position": v(2.92, 46) * mm});
            skCircle(sketch, "E268.cCircle", {"center": v(-15, 15) * mm, "radius": 2.92 * mm, "construction": true});
            skLineSegment(sketch, "E268.0", {"start": v(-12.08, 16.68) * mm, "end": v(-12.08, 13.32) * mm});
            skLineSegment(sketch, "E268.1", {"start": v(-12.08, 13.32) * mm, "end": v(-15, 11.63) * mm, "construction": true});
            skLineSegment(sketch, "E268.2", {"start": v(-15, 11.63) * mm, "end": v(-17.92, 13.32) * mm, "construction": true});
            skLineSegment(sketch, "E268.3", {"start": v(-17.92, 13.32) * mm, "end": v(-17.92, 16.68) * mm});
            skLineSegment(sketch, "E268.4", {"start": v(-17.92, 16.68) * mm, "end": v(-15, 18.37) * mm});
            skLineSegment(sketch, "E268.5", {"start": v(-15, 18.37) * mm, "end": v(-12.08, 16.68) * mm});
            skPoint(sketch, "E268.0.midPoint", {"position": v(-12.08, 15) * mm});
            skLineSegment(sketch, "E269", {"start": v(-2.92, 47.68) * mm, "end": v(-2.92, 59.05) * mm});
            skLineSegment(sketch, "E270", {"start": v(-2.92, 59.05) * mm, "end": v(0, 59.05) * mm});
            skLineSegment(sketch, "E271.MirrorCS", {"start": v(2.92, 59.05) * mm, "end": v(0, 59.05) * mm});
            skLineSegment(sketch, "E272.MirrorCS", {"start": v(2.92, 47.68) * mm, "end": v(2.92, 59.05) * mm});
            skLineSegment(sketch, "E273", {"start": v(-17.92, 13.32) * mm, "end": v(-17.92, 0) * mm});
            skLineSegment(sketch, "E274", {"start": v(-17.92, 0) * mm, "end": v(-12.08, 0) * mm});
            skLineSegment(sketch, "E275", {"start": v(-12.08, 0) * mm, "end": v(-12.08, 13.32) * mm});
            skLineSegment(sketch, "E276.MirrorCS", {"start": v(12.08, 16.68) * mm, "end": v(12.08, 13.32) * mm});
            skCircle(sketch, "E277.MirrorC", {"center": v(15, 15) * mm, "radius": 2.92 * mm, "construction": true});
            skLineSegment(sketch, "E278.MirrorCS", {"start": v(15, 11.63) * mm, "end": v(17.92, 13.32) * mm, "construction": true});
            skLineSegment(sketch, "E279.MirrorCS", {"start": v(12.08, 13.32) * mm, "end": v(15, 11.63) * mm, "construction": true});
            skLineSegment(sketch, "E280.MirrorCS", {"start": v(17.92, 16.68) * mm, "end": v(15, 18.37) * mm});
            skLineSegment(sketch, "E281.MirrorCS", {"start": v(17.92, 13.32) * mm, "end": v(17.92, 16.68) * mm});
            skLineSegment(sketch, "E282.MirrorCS", {"start": v(17.92, 0) * mm, "end": v(12.08, 0) * mm});
            skLineSegment(sketch, "E283.MirrorCS", {"start": v(12.08, 0) * mm, "end": v(12.08, 13.32) * mm});
            skLineSegment(sketch, "E284.MirrorCS", {"start": v(15, 18.37) * mm, "end": v(12.08, 16.68) * mm});
            skPoint(sketch, "E285.MirrorP", {"position": v(12.08, 15) * mm});
            skLineSegment(sketch, "E286.MirrorCS", {"start": v(17.92, 13.32) * mm, "end": v(17.92, 0) * mm});
            skSolve(sketch);
        }
        {
            var Q0;
            Q0=qSketchRegion(id+"F43",true);
            extrude(context, id + "F44", {"entities" : qUnion([Q0]), "operationType" : NewBodyOperationType.REMOVE, "depth" : 4 * mm});
        }
        {
            var Q0;
            Q0=qCreatedBy(id+"F42.planeOp",FACE);
            var sketch = newSketch(context, id + "F45", { "sketchPlane" : qUnion([Q0])});
            skCircle(sketch, "E287", {"center": v(-15, 15) * mm, "radius": 2.12 * mm});
            skCircle(sketch, "E288", {"center": v(0, 46) * mm, "radius": 2.12 * mm});
            skCircle(sketch, "E289.MirrorC", {"center": v(15, 15) * mm, "radius": 2.12 * mm});
            skSolve(sketch);
        }
        {
            var Q0;
            Q0=qSketchRegion(id+"F45",true);
            extrude(context, id + "F46", {"entities" : qUnion([Q0]), "operationType" : NewBodyOperationType.REMOVE, "depth" : 25 * mm});
        }
        {
            var Q0;
            Q0=qCreatedBy(makeId("Top.planeOp"),FACE);
            var sketch = newSketch(context, id + "F47", { "sketchPlane" : qUnion([Q0])});
            skCircle(sketch, "E290.cCircle", {"center": v(-30, 24) * mm, "radius": 5.54 * mm, "construction": true});
            skLineSegment(sketch, "E290.0", {"start": v(-33.2, 29.54) * mm, "end": v(-26.8, 29.54) * mm});
            skLineSegment(sketch, "E290.1", {"start": v(-26.8, 29.54) * mm, "end": v(-23.6, 24) * mm});
            skLineSegment(sketch, "E290.2", {"start": v(-23.6, 24) * mm, "end": v(-26.8, 18.46) * mm});
            skLineSegment(sketch, "E290.3", {"start": v(-26.8, 18.46) * mm, "end": v(-33.2, 18.46) * mm});
            skLineSegment(sketch, "E290.4", {"start": v(-33.2, 18.46) * mm, "end": v(-36.4, 24) * mm});
            skLineSegment(sketch, "E290.5", {"start": v(-36.4, 24) * mm, "end": v(-33.2, 29.54) * mm});
            skPoint(sketch, "E290.0.midPoint", {"position": v(-30, 29.54) * mm});
            skCircle(sketch, "E291", {"center": v(-30, 24) * mm, "radius": 2.12 * mm});
            skLineSegment(sketch, "E292.MirrorCS", {"start": v(26.8, 18.46) * mm, "end": v(33.2, 18.46) * mm});
            skLineSegment(sketch, "E293.MirrorCS", {"start": v(33.2, 29.54) * mm, "end": v(26.8, 29.54) * mm});
            skLineSegment(sketch, "E294.MirrorCS", {"start": v(26.8, 29.54) * mm, "end": v(23.6, 24) * mm});
            skCircle(sketch, "E295.MirrorC", {"center": v(30, 24) * mm, "radius": 5.54 * mm, "construction": true});
            skPoint(sketch, "E296.MirrorP", {"position": v(30, 29.54) * mm});
            skLineSegment(sketch, "E297.MirrorCS", {"start": v(33.2, 18.46) * mm, "end": v(36.4, 24) * mm});
            skLineSegment(sketch, "E298.MirrorCS", {"start": v(36.4, 24) * mm, "end": v(33.2, 29.54) * mm});
            skCircle(sketch, "E299.MirrorC", {"center": v(30, 24) * mm, "radius": 2.12 * mm});
            skLineSegment(sketch, "E300.MirrorCS", {"start": v(23.6, 24) * mm, "end": v(26.8, 18.46) * mm});
            skLineSegment(sketch, "E301.MirrorCS", {"start": v(33.2, -18.46) * mm, "end": v(36.4, -24) * mm});
            skLineSegment(sketch, "E302.MirrorCS", {"start": v(26.8, -29.54) * mm, "end": v(23.6, -24) * mm});
            skCircle(sketch, "E303.MirrorC", {"center": v(30, -24) * mm, "radius": 5.54 * mm, "construction": true});
            skPoint(sketch, "E304.MirrorP", {"position": v(30, -29.54) * mm});
            skLineSegment(sketch, "E305.MirrorCS", {"start": v(-33.2, -29.54) * mm, "end": v(-26.8, -29.54) * mm});
            skLineSegment(sketch, "E306.MirrorCS", {"start": v(-26.8, -29.54) * mm, "end": v(-23.6, -24) * mm});
            skCircle(sketch, "E307.MirrorC", {"center": v(-30, -24) * mm, "radius": 5.54 * mm, "construction": true});
            skLineSegment(sketch, "E308.MirrorCS", {"start": v(23.6, -24) * mm, "end": v(26.8, -18.46) * mm});
            skLineSegment(sketch, "E309.MirrorCS", {"start": v(36.4, -24) * mm, "end": v(33.2, -29.54) * mm});
            skCircle(sketch, "E310.MirrorC", {"center": v(30, -24) * mm, "radius": 2.12 * mm});
            skLineSegment(sketch, "E311.MirrorCS", {"start": v(33.2, -29.54) * mm, "end": v(26.8, -29.54) * mm});
            skPoint(sketch, "E312.MirrorP", {"position": v(-30, -29.54) * mm});
            skLineSegment(sketch, "E313.MirrorCS", {"start": v(26.8, -18.46) * mm, "end": v(33.2, -18.46) * mm});
            skLineSegment(sketch, "E314.MirrorCS", {"start": v(-26.8, -18.46) * mm, "end": v(-33.2, -18.46) * mm});
            skLineSegment(sketch, "E315.MirrorCS", {"start": v(-36.4, -24) * mm, "end": v(-33.2, -29.54) * mm});
            skLineSegment(sketch, "E316.MirrorCS", {"start": v(-33.2, -18.46) * mm, "end": v(-36.4, -24) * mm});
            skLineSegment(sketch, "E317.MirrorCS", {"start": v(-23.6, -24) * mm, "end": v(-26.8, -18.46) * mm});
            skCircle(sketch, "E318.MirrorC", {"center": v(-30, -24) * mm, "radius": 2.12 * mm});
            skSolve(sketch);
        }
        {
            var Q0;
            Q0=qSketchRegion(id+"F47",true);
            extrude(context, id + "F48", {"entities" : qUnion([Q0]), "operationType" : NewBodyOperationType.ADD, "depth" : 5 * mm});
        }
        {
            var Q0;
            Q0=makeQuery(id+"F48.opExtrude","CAP_FACE",FACE,{"disambiguationData":[OSD([sQuery(id+"F47.wireOp",EDGE,"E305.MirrorCS"),sQuery(id+"F47.wireOp",EDGE,"E306.MirrorCS"),sQuery(id+"F47.wireOp",EDGE,"E314.MirrorCS"),sQuery(id+"F47.wireOp",EDGE,"E315.MirrorCS"),sQuery(id+"F47.wireOp",EDGE,"E316.MirrorCS"),sQuery(id+"F47.wireOp",EDGE,"E317.MirrorCS"),sQuery(id+"F47.wireOp",EDGE,"E318.MirrorC")])],"isStart":false});
            var sketch = newSketch(context, id + "F49", { "sketchPlane" : qUnion([Q0])});
            skCircle(sketch, "E319.cCircle", {"center": v(-30, -24) * mm, "radius": 5.54 * mm, "construction": true});
            skLineSegment(sketch, "E319.0", {"start": v(-33.2, -18.46) * mm, "end": v(-26.8, -18.46) * mm});
            skLineSegment(sketch, "E319.1", {"start": v(-26.8, -18.46) * mm, "end": v(-23.6, -24) * mm});
            skLineSegment(sketch, "E319.2", {"start": v(-23.6, -24) * mm, "end": v(-26.8, -29.54) * mm});
            skLineSegment(sketch, "E319.3", {"start": v(-26.8, -29.54) * mm, "end": v(-33.2, -29.54) * mm});
            skLineSegment(sketch, "E319.4", {"start": v(-33.2, -29.54) * mm, "end": v(-36.4, -24) * mm});
            skLineSegment(sketch, "E319.5", {"start": v(-36.4, -24) * mm, "end": v(-33.2, -18.46) * mm});
            skPoint(sketch, "E319.0.midPoint", {"position": v(-30, -18.46) * mm});
            skCircle(sketch, "E320.cCircle", {"center": v(-30, -24) * mm, "radius": 2.92 * mm, "construction": true});
            skLineSegment(sketch, "E320.0", {"start": v(-31.68, -21.08) * mm, "end": v(-28.32, -21.08) * mm});
            skLineSegment(sketch, "E320.1", {"start": v(-28.32, -21.08) * mm, "end": v(-26.63, -24) * mm});
            skLineSegment(sketch, "E320.2", {"start": v(-26.63, -24) * mm, "end": v(-28.32, -26.92) * mm});
            skLineSegment(sketch, "E320.3", {"start": v(-28.32, -26.92) * mm, "end": v(-31.68, -26.92) * mm});
            skLineSegment(sketch, "E320.4", {"start": v(-31.68, -26.92) * mm, "end": v(-33.37, -24) * mm});
            skLineSegment(sketch, "E320.5", {"start": v(-33.37, -24) * mm, "end": v(-31.68, -21.08) * mm});
            skPoint(sketch, "E320.0.midPoint", {"position": v(-30, -21.08) * mm});
            skLineSegment(sketch, "E321.MirrorCS", {"start": v(31.68, -21.08) * mm, "end": v(28.32, -21.08) * mm});
            skLineSegment(sketch, "E322.MirrorCS", {"start": v(26.8, -29.54) * mm, "end": v(33.2, -29.54) * mm});
            skLineSegment(sketch, "E323.MirrorCS", {"start": v(23.6, -24) * mm, "end": v(26.8, -29.54) * mm});
            skCircle(sketch, "E324.MirrorC", {"center": v(30, -24) * mm, "radius": 2.92 * mm, "construction": true});
            skLineSegment(sketch, "E325.MirrorCS", {"start": v(28.32, -21.08) * mm, "end": v(26.63, -24) * mm});
            skLineSegment(sketch, "E326.MirrorCS", {"start": v(33.37, -24) * mm, "end": v(31.68, -21.08) * mm});
            skLineSegment(sketch, "E327.MirrorCS", {"start": v(33.2, -29.54) * mm, "end": v(36.4, -24) * mm});
            skLineSegment(sketch, "E328.MirrorCS", {"start": v(26.63, -24) * mm, "end": v(28.32, -26.92) * mm});
            skLineSegment(sketch, "E329.MirrorCS", {"start": v(26.8, -18.46) * mm, "end": v(23.6, -24) * mm});
            skLineSegment(sketch, "E330.MirrorCS", {"start": v(33.2, -18.46) * mm, "end": v(26.8, -18.46) * mm});
            skPoint(sketch, "E331.MirrorP", {"position": v(30, -18.46) * mm});
            skLineSegment(sketch, "E332.MirrorCS", {"start": v(28.32, -26.92) * mm, "end": v(31.68, -26.92) * mm});
            skLineSegment(sketch, "E333.MirrorCS", {"start": v(36.4, -24) * mm, "end": v(33.2, -18.46) * mm});
            skLineSegment(sketch, "E334.MirrorCS", {"start": v(31.68, -26.92) * mm, "end": v(33.37, -24) * mm});
            skPoint(sketch, "E335.MirrorP", {"position": v(30, -21.08) * mm});
            skCircle(sketch, "E336.MirrorC", {"center": v(30, -24) * mm, "radius": 5.54 * mm, "construction": true});
            skCircle(sketch, "E337.MirrorC", {"center": v(30, 24) * mm, "radius": 5.54 * mm, "construction": true});
            skLineSegment(sketch, "E338.MirrorCS", {"start": v(-28.32, 26.92) * mm, "end": v(-31.68, 26.92) * mm});
            skLineSegment(sketch, "E339.MirrorCS", {"start": v(23.6, 24) * mm, "end": v(26.8, 29.54) * mm});
            skLineSegment(sketch, "E340.MirrorCS", {"start": v(-31.68, 26.92) * mm, "end": v(-33.37, 24) * mm});
            skLineSegment(sketch, "E341.MirrorCS", {"start": v(-28.32, 21.08) * mm, "end": v(-26.63, 24) * mm});
            skLineSegment(sketch, "E342.MirrorCS", {"start": v(28.32, 21.08) * mm, "end": v(26.63, 24) * mm});
            skLineSegment(sketch, "E343.MirrorCS", {"start": v(-26.63, 24) * mm, "end": v(-28.32, 26.92) * mm});
            skLineSegment(sketch, "E344.MirrorCS", {"start": v(33.2, 29.54) * mm, "end": v(36.4, 24) * mm});
            skLineSegment(sketch, "E345.MirrorCS", {"start": v(26.8, 18.46) * mm, "end": v(23.6, 24) * mm});
            skCircle(sketch, "E346.MirrorC", {"center": v(-30, 24) * mm, "radius": 5.54 * mm, "construction": true});
            skLineSegment(sketch, "E347.MirrorCS", {"start": v(-33.2, 18.46) * mm, "end": v(-26.8, 18.46) * mm});
            skLineSegment(sketch, "E348.MirrorCS", {"start": v(31.68, 26.92) * mm, "end": v(33.37, 24) * mm});
            skPoint(sketch, "E349.MirrorP", {"position": v(30, 18.46) * mm});
            skLineSegment(sketch, "E350.MirrorCS", {"start": v(26.63, 24) * mm, "end": v(28.32, 26.92) * mm});
            skLineSegment(sketch, "E351.MirrorCS", {"start": v(-36.4, 24) * mm, "end": v(-33.2, 18.46) * mm});
            skLineSegment(sketch, "E352.MirrorCS", {"start": v(-23.6, 24) * mm, "end": v(-26.8, 29.54) * mm});
            skPoint(sketch, "E353.MirrorP", {"position": v(-30, 18.46) * mm});
            skLineSegment(sketch, "E354.MirrorCS", {"start": v(26.8, 29.54) * mm, "end": v(33.2, 29.54) * mm});
            skLineSegment(sketch, "E355.MirrorCS", {"start": v(-31.68, 21.08) * mm, "end": v(-28.32, 21.08) * mm});
            skCircle(sketch, "E356.MirrorC", {"center": v(30, 24) * mm, "radius": 2.92 * mm, "construction": true});
            skLineSegment(sketch, "E357.MirrorCS", {"start": v(31.68, 21.08) * mm, "end": v(28.32, 21.08) * mm});
            skPoint(sketch, "E358.MirrorP", {"position": v(-30, 21.08) * mm});
            skLineSegment(sketch, "E359.MirrorCS", {"start": v(-33.2, 29.54) * mm, "end": v(-36.4, 24) * mm});
            skLineSegment(sketch, "E360.MirrorCS", {"start": v(-26.8, 18.46) * mm, "end": v(-23.6, 24) * mm});
            skPoint(sketch, "E361.MirrorP", {"position": v(30, 21.08) * mm});
            skLineSegment(sketch, "E362.MirrorCS", {"start": v(33.37, 24) * mm, "end": v(31.68, 21.08) * mm});
            skLineSegment(sketch, "E363.MirrorCS", {"start": v(33.2, 18.46) * mm, "end": v(26.8, 18.46) * mm});
            skLineSegment(sketch, "E364.MirrorCS", {"start": v(-33.37, 24) * mm, "end": v(-31.68, 21.08) * mm});
            skLineSegment(sketch, "E365.MirrorCS", {"start": v(-26.8, 29.54) * mm, "end": v(-33.2, 29.54) * mm});
            skLineSegment(sketch, "E366.MirrorCS", {"start": v(36.4, 24) * mm, "end": v(33.2, 18.46) * mm});
            skLineSegment(sketch, "E367.MirrorCS", {"start": v(28.32, 26.92) * mm, "end": v(31.68, 26.92) * mm});
            skCircle(sketch, "E368.MirrorC", {"center": v(-30, 24) * mm, "radius": 2.92 * mm, "construction": true});
            skSolve(sketch);
        }
        {
            var Q0;
            Q0 = qSketchRegion(id + "F49", true);
            extrude(context, id + "F50", {"entities" : qUnion([Q0]), "operationType" : NewBodyOperationType.ADD, "depth" : 4 * mm});
        }
        {
            var Q0;
            Q0=makeQuery(id+"F50.opExtrude","CAP_FACE",FACE,{"disambiguationData":[OSD([sQuery(id+"F49.wireOp",EDGE,"E319.0"),sQuery(id+"F49.wireOp",EDGE,"E319.1"),sQuery(id+"F49.wireOp",EDGE,"E319.2"),sQuery(id+"F49.wireOp",EDGE,"E319.3"),sQuery(id+"F49.wireOp",EDGE,"E319.4"),sQuery(id+"F49.wireOp",EDGE,"E319.5"),sQuery(id+"F49.wireOp",EDGE,"E320.0"),sQuery(id+"F49.wireOp",EDGE,"E320.1"),sQuery(id+"F49.wireOp",EDGE,"E320.2"),sQuery(id+"F49.wireOp",EDGE,"E320.3"),sQuery(id+"F49.wireOp",EDGE,"E320.4"),sQuery(id+"F49.wireOp",EDGE,"E320.5")])],"isStart":false});
            var sketch = newSketch(context, id + "F51", { "sketchPlane" : qUnion([Q0])});
            skLineSegment(sketch, "E369.bottom", {"start": v(-54.15, 24) * mm, "end": v(53.3, 24) * mm});
            skLineSegment(sketch, "E369.top", {"start": v(-54.15, -24) * mm, "end": v(53.3, -24) * mm});
            skLineSegment(sketch, "E369.left", {"start": v(-54.15, 24) * mm, "end": v(-54.15, -24) * mm});
            skLineSegment(sketch, "E369.right", {"start": v(53.3, 24) * mm, "end": v(53.3, -24) * mm});
            skSolve(sketch);
        }
        {
            var Q0;
            Q0 = qSketchRegion(id + "F51", true);
            extrude(context, id + "F52", {"entities" : qUnion([Q0]), "operationType" : NewBodyOperationType.REMOVE, "endBound" : BoundingType.THROUGH_ALL, "depth" : 25 * mm});
        }
        {
            var Q0;
            Q0=qCreatedBy(makeId("Top.planeOp"),FACE);
            var sketch = newSketch(context, id + "F53", { "sketchPlane" : qUnion([Q0])});
            skLineSegment(sketch, "E370.bottom", {"start": v(-17.2, -24) * mm, "end": v(-12.2, -24) * mm});
            skLineSegment(sketch, "E370.top", {"start": v(-17.2, -24) * mm, "end": v(-12.2, -24) * mm});
            skLineSegment(sketch, "E370.left", {"start": v(-17.2, -24) * mm, "end": v(-17.2, -24) * mm});
            skLineSegment(sketch, "E370.right", {"start": v(-12.2, -24) * mm, "end": v(-12.2, -24) * mm});
            skLineSegment(sketch, "E371.bottom", {"start": v(-54.15, 24) * mm, "end": v(-59.15, 24) * mm});
            skLineSegment(sketch, "E371.top", {"start": v(-54.15, -24) * mm, "end": v(-59.15, -24) * mm});
            skLineSegment(sketch, "E371.left", {"start": v(-54.15, 24) * mm, "end": v(-54.15, -24) * mm});
            skLineSegment(sketch, "E371.right", {"start": v(-59.15, 24) * mm, "end": v(-59.15, -24) * mm});
            skSolve(sketch);
        }
        {
            var Q0;
            Q0 = qSketchRegion(id + "F53", true);
            extrude(context, id + "F54", {"entities" : qUnion([Q0]), "operationType" : NewBodyOperationType.ADD, "depth" : 9 * mm});
        }
        {
            var Q0;
            Q0=makeQuery(id+"F54.opExtrude","SWEPT_EDGE",EDGE,{"disambiguationData":[OSD([sQuery(id+"F53.wireOp",EDGE,"E371.top"),sQuery(id+"F53.wireOp",EDGE,"E371.right")])]});
            var Q1;
            Q1=makeQuery(id+"F54.opExtrude","SWEPT_EDGE",EDGE,{"disambiguationData":[OSD([sQuery(id+"F53.wireOp",EDGE,"E371.bottom"),sQuery(id+"F53.wireOp",EDGE,"E371.right")])]});
            fillet(context, id + "F55", {"entities" : qUnion([Q0, Q1]), "radius" : 2.5 * mm, "tangentPropagation" : true, "allowEdgeOverflow" : false});
        }
        {
            var Q0;
            Q0=qCreatedBy(makeId("Top.planeOp"),FACE);
            var sketch = newSketch(context, id + "F56", { "sketchPlane" : qUnion([Q0])});
            skLineSegment(sketch, "E372.bottom", {"start": v(53.3, 24) * mm, "end": v(113.3, 24) * mm});
            skLineSegment(sketch, "E372.top", {"start": v(53.3, -24) * mm, "end": v(113.3, -24) * mm});
            skLineSegment(sketch, "E372.left", {"start": v(53.3, 24) * mm, "end": v(53.3, -24) * mm});
            skLineSegment(sketch, "E372.right", {"start": v(113.3, 24) * mm, "end": v(113.3, -24) * mm});
            skArc(sketch, "E373", {"start": v(96.58, 10.5) * mm, "mid": v(93.3, 11) * mm, "end": v(90, 10.5) * mm});
            skCircle(sketch, "E374.cCircle", {"center": v(104.03, 0) * mm, "radius": 2.08 * mm, "construction": true});
            skLineSegment(sketch, "E374.0", {"start": v(106.1, 1.2) * mm, "end": v(106.1, -1.2) * mm});
            skLineSegment(sketch, "E374.1", {"start": v(106.1, -1.2) * mm, "end": v(104.03, -2.4) * mm});
            skLineSegment(sketch, "E374.2", {"start": v(104.03, -2.4) * mm, "end": v(101.95, -1.2) * mm, "construction": true});
            skLineSegment(sketch, "E374.3", {"start": v(101.95, -1.2) * mm, "end": v(101.95, 1.2) * mm, "construction": true});
            skLineSegment(sketch, "E374.4", {"start": v(101.95, 1.2) * mm, "end": v(104.03, 2.4) * mm, "construction": true});
            skLineSegment(sketch, "E374.5", {"start": v(104.03, 2.4) * mm, "end": v(106.1, 1.2) * mm});
            skPoint(sketch, "E374.0.midPoint", {"position": v(106.1, 0) * mm});
            skLineSegment(sketch, "E375.1.0", {"start": v(96.58, 8.1) * mm, "end": v(96.58, 10.5) * mm, "construction": true});
            skLineSegment(sketch, "E375.1.1", {"start": v(98.66, 6.9) * mm, "end": v(96.58, 8.1) * mm, "construction": true});
            skLineSegment(sketch, "E375.1.2", {"start": v(100.74, 8.1) * mm, "end": v(98.66, 6.9) * mm, "construction": true});
            skLineSegment(sketch, "E375.1.3", {"start": v(96.58, 10.5) * mm, "end": v(98.66, 11.7) * mm});
            skLineSegment(sketch, "E375.1.4", {"start": v(98.66, 11.7) * mm, "end": v(100.74, 10.5) * mm});
            skLineSegment(sketch, "E375.1.5", {"start": v(100.74, 10.5) * mm, "end": v(100.74, 8.1) * mm});
            skLineSegment(sketch, "E375.2.0", {"start": v(87.93, 6.9) * mm, "end": v(85.85, 8.1) * mm, "construction": true});
            skLineSegment(sketch, "E375.2.1", {"start": v(90, 8.1) * mm, "end": v(87.93, 6.9) * mm, "construction": true});
            skLineSegment(sketch, "E375.2.2", {"start": v(90, 10.5) * mm, "end": v(90, 8.1) * mm, "construction": true});
            skLineSegment(sketch, "E375.2.3", {"start": v(85.85, 8.1) * mm, "end": v(85.85, 10.5) * mm});
            skLineSegment(sketch, "E375.2.4", {"start": v(85.85, 10.5) * mm, "end": v(87.93, 11.7) * mm});
            skLineSegment(sketch, "E375.2.5", {"start": v(87.93, 11.7) * mm, "end": v(90, 10.5) * mm});
            skLineSegment(sketch, "E375.3.0", {"start": v(84.64, -1.2) * mm, "end": v(82.56, -2.4) * mm, "construction": true});
            skLineSegment(sketch, "E375.3.1", {"start": v(84.64, 1.2) * mm, "end": v(84.64, -1.2) * mm, "construction": true});
            skLineSegment(sketch, "E375.3.2", {"start": v(82.56, 2.4) * mm, "end": v(84.64, 1.2) * mm, "construction": true});
            skLineSegment(sketch, "E375.3.3", {"start": v(82.56, -2.4) * mm, "end": v(80.48, -1.2) * mm});
            skLineSegment(sketch, "E375.3.4", {"start": v(80.48, -1.2) * mm, "end": v(80.48, 1.2) * mm});
            skLineSegment(sketch, "E375.3.5", {"start": v(80.48, 1.2) * mm, "end": v(82.56, 2.4) * mm});
            skLineSegment(sketch, "E375.4.0", {"start": v(90, -8.1) * mm, "end": v(90, -10.5) * mm, "construction": true});
            skLineSegment(sketch, "E375.4.1", {"start": v(87.93, -6.9) * mm, "end": v(90, -8.1) * mm, "construction": true});
            skLineSegment(sketch, "E375.4.2", {"start": v(85.85, -8.1) * mm, "end": v(87.93, -6.9) * mm, "construction": true});
            skLineSegment(sketch, "E375.4.3", {"start": v(90, -10.5) * mm, "end": v(87.93, -11.7) * mm});
            skLineSegment(sketch, "E375.4.4", {"start": v(87.93, -11.7) * mm, "end": v(85.85, -10.5) * mm});
            skLineSegment(sketch, "E375.4.5", {"start": v(85.85, -10.5) * mm, "end": v(85.85, -8.1) * mm});
            skLineSegment(sketch, "E375.5.0", {"start": v(98.66, -6.9) * mm, "end": v(100.74, -8.1) * mm, "construction": true});
            skLineSegment(sketch, "E375.5.1", {"start": v(96.58, -8.1) * mm, "end": v(98.66, -6.9) * mm, "construction": true});
            skLineSegment(sketch, "E375.5.2", {"start": v(96.58, -10.5) * mm, "end": v(96.58, -8.1) * mm, "construction": true});
            skLineSegment(sketch, "E375.5.3", {"start": v(100.74, -8.1) * mm, "end": v(100.74, -10.5) * mm});
            skLineSegment(sketch, "E375.5.4", {"start": v(100.74, -10.5) * mm, "end": v(98.66, -11.7) * mm});
            skLineSegment(sketch, "E375.5.5", {"start": v(98.66, -11.7) * mm, "end": v(96.58, -10.5) * mm});
            skArc(sketch, "E376.trimOffspring", {"start": v(85.85, 8.1) * mm, "mid": v(83.77, 5.5) * mm, "end": v(82.56, 2.4) * mm});
            skArc(sketch, "E377.trimOffspring", {"start": v(82.56, -2.4) * mm, "mid": v(83.77, -5.5) * mm, "end": v(85.85, -8.1) * mm});
            skArc(sketch, "E378.trimOffspring", {"start": v(90, -10.5) * mm, "mid": v(93.3, -11) * mm, "end": v(96.58, -10.5) * mm});
            skArc(sketch, "E379.trimOffspring", {"start": v(100.74, -8.1) * mm, "mid": v(102.82, -5.5) * mm, "end": v(104.03, -2.4) * mm});
            skArc(sketch, "E380.trimOffspring", {"start": v(104.03, 2.4) * mm, "mid": v(102.82, 5.5) * mm, "end": v(100.74, 8.1) * mm});
            skSolve(sketch);
        }
        {
            var Q0;
            Q0 = qSketchRegion(id + "F56", true);
            extrude(context, id + "F57", {"entities" : qUnion([Q0]), "operationType" : NewBodyOperationType.ADD, "depth" : 9 * mm});
        }
        {
            var Q0;
            Q0=makeQuery(id+"F57.opExtrude","SWEPT_EDGE",EDGE,{"disambiguationData":[OSD([sQuery(id+"F56.wireOp",EDGE,"E372.top"),sQuery(id+"F56.wireOp",EDGE,"E372.right")])]});
            var Q1;
            Q1=makeQuery(id+"F57.opExtrude","SWEPT_EDGE",EDGE,{"disambiguationData":[OSD([sQuery(id+"F56.wireOp",EDGE,"E372.bottom"),sQuery(id+"F56.wireOp",EDGE,"E372.right")])]});
            chamfer(context, id + "F58", {"entities" : qUnion([Q0, Q1]), "width" : 1.75 * mm, "tangentPropagation" : true});
        }
        {
            var Q0;
            Q0=qCreatedBy(makeId("Top.planeOp"),FACE);
            var sketch = newSketch(context, id + "F59", { "sketchPlane" : qUnion([Q0])});
            skLineSegment(sketch, "E381.bottom", {"start": v(-49.65, 20.92) * mm, "end": v(-45.65, 20.92) * mm});
            skLineSegment(sketch, "E381.top", {"start": v(-49.65, 15.08) * mm, "end": v(-45.65, 15.08) * mm});
            skLineSegment(sketch, "E381.left", {"start": v(-49.65, 20.92) * mm, "end": v(-49.65, 15.08) * mm});
            skLineSegment(sketch, "E381.right", {"start": v(-45.65, 20.92) * mm, "end": v(-45.65, 15.08) * mm});
            skLineSegment(sketch, "E382.MirrorCS", {"start": v(-49.65, -20.92) * mm, "end": v(-45.65, -20.92) * mm});
            skLineSegment(sketch, "E383.MirrorCS", {"start": v(-49.65, -20.92) * mm, "end": v(-49.65, -15.08) * mm});
            skLineSegment(sketch, "E384.MirrorCS", {"start": v(-45.65, -20.92) * mm, "end": v(-45.65, -15.08) * mm});
            skLineSegment(sketch, "E385.MirrorCS", {"start": v(-49.65, -15.08) * mm, "end": v(-45.65, -15.08) * mm});
            skLineSegment(sketch, "E386.bottom", {"start": v(47, 17.92) * mm, "end": v(51, 17.92) * mm});
            skLineSegment(sketch, "E386.top", {"start": v(47, 12.08) * mm, "end": v(51, 12.08) * mm});
            skLineSegment(sketch, "E386.left", {"start": v(47, 17.92) * mm, "end": v(47, 12.08) * mm});
            skLineSegment(sketch, "E386.right", {"start": v(51, 17.92) * mm, "end": v(51, 12.08) * mm});
            skLineSegment(sketch, "E387.MirrorCS", {"start": v(47, -17.92) * mm, "end": v(51, -17.92) * mm});
            skLineSegment(sketch, "E388.MirrorCS", {"start": v(47, -12.08) * mm, "end": v(51, -12.08) * mm});
            skLineSegment(sketch, "E389.MirrorCS", {"start": v(51, -17.92) * mm, "end": v(51, -12.08) * mm});
            skLineSegment(sketch, "E390.MirrorCS", {"start": v(47, -17.92) * mm, "end": v(47, -12.08) * mm});
            skSolve(sketch);
        }
        {
            var Q0;
            Q0 = qSketchRegion(id + "F59", true);
            extrude(context, id + "F60", {"entities" : qUnion([Q0]), "operationType" : NewBodyOperationType.ADD, "depth" : 9 * mm});
        }
        {
            var Q0;
            {var subQ2=sQuery(id+"F51.wireOp",EDGE,"E369.bottom");Q0=makeQuery(id+"F54.boolean.opBoolean","MERGE",EDGE,{"derivedFrom":[makeQuery(id+"F52.boolean.opBoolean","COPY",EDGE,{"disambiguationData":[TD([makeQuery(id+"F1.opExtrude","SWEPT_FACE",FACE,{"disambiguationData":[OSD([sQuery(id+"F0.wireOp",EDGE,"E78")])]})])],"derivedFrom":makeQuery(id+"F52.opExtrude","CAP_EDGE",EDGE,{"disambiguationData":[OSD([subQ2])],"isStart":true})}),makeQuery(id+"F54.opExtrude","CAP_EDGE",EDGE,{"disambiguationData":[OSD([sQuery(id+"F53.wireOp",EDGE,"E371.bottom")])],"isStart":false})]});}
            var Q1;
            Q1=makeQuery(id+"F54.opExtrude","CAP_EDGE",EDGE,{"disambiguationData":[OSD([sQuery(id+"F53.wireOp",EDGE,"E371.right")])],"isStart":false});
            var Q2;
            {var subQ2=sQuery(id+"F51.wireOp",EDGE,"E369.top");Q2=makeQuery(id+"F54.boolean.opBoolean","MERGE",EDGE,{"derivedFrom":[makeQuery(id+"F52.boolean.opBoolean","COPY",EDGE,{"disambiguationData":[TD([makeQuery(id+"F1.opExtrude","SWEPT_FACE",FACE,{"disambiguationData":[OSD([sQuery(id+"F0.wireOp",EDGE,"E78")])]})])],"derivedFrom":makeQuery(id+"F52.opExtrude","CAP_EDGE",EDGE,{"disambiguationData":[OSD([subQ2])],"isStart":true})}),makeQuery(id+"F54.opExtrude","CAP_EDGE",EDGE,{"disambiguationData":[OSD([sQuery(id+"F53.wireOp",EDGE,"E371.top")])],"isStart":false})]});}
            var Q3;
            {var subQ0=sQuery(id+"F53.wireOp",EDGE,"E371.right");var subQ1=sQuery(id+"F53.wireOp",EDGE,"E371.bottom");Q3=makeQuery(id+"F55.opFillet","BLEND_EDGE",EDGE,{"blendedFrom":[makeQuery(id+"F54.opExtrude","SWEPT_EDGE",EDGE,{"disambiguationData":[OSD([subQ1,subQ0])]}),makeQuery(id+"F54.boolean.opBoolean","MERGE",FACE,{"derivedFrom":[makeQuery(id+"F52.boolean.opBoolean","MERGE",FACE,{"derivedFrom":[makeQuery(id+"F50.opExtrude","CAP_FACE",FACE,{"disambiguationData":[OSD([sQuery(id+"F49.wireOp",EDGE,"E319.0"),sQuery(id+"F49.wireOp",EDGE,"E319.1"),sQuery(id+"F49.wireOp",EDGE,"E319.2"),sQuery(id+"F49.wireOp",EDGE,"E319.3"),sQuery(id+"F49.wireOp",EDGE,"E319.4"),sQuery(id+"F49.wireOp",EDGE,"E319.5"),sQuery(id+"F49.wireOp",EDGE,"E320.0"),sQuery(id+"F49.wireOp",EDGE,"E320.1"),sQuery(id+"F49.wireOp",EDGE,"E320.2"),sQuery(id+"F49.wireOp",EDGE,"E320.3"),sQuery(id+"F49.wireOp",EDGE,"E320.4"),sQuery(id+"F49.wireOp",EDGE,"E320.5")])],"isStart":false}),makeQuery(id+"F50.opExtrude","CAP_FACE",FACE,{"disambiguationData":[OSD([sQuery(id+"F49.wireOp",EDGE,"E321.MirrorCS"),sQuery(id+"F49.wireOp",EDGE,"E322.MirrorCS"),sQuery(id+"F49.wireOp",EDGE,"E323.MirrorCS"),sQuery(id+"F49.wireOp",EDGE,"E325.MirrorCS"),sQuery(id+"F49.wireOp",EDGE,"E326.MirrorCS"),sQuery(id+"F49.wireOp",EDGE,"E327.MirrorCS"),sQuery(id+"F49.wireOp",EDGE,"E328.MirrorCS"),sQuery(id+"F49.wireOp",EDGE,"E329.MirrorCS"),sQuery(id+"F49.wireOp",EDGE,"E330.MirrorCS"),sQuery(id+"F49.wireOp",EDGE,"E332.MirrorCS"),sQuery(id+"F49.wireOp",EDGE,"E333.MirrorCS"),sQuery(id+"F49.wireOp",EDGE,"E334.MirrorCS")])],"isStart":false}),makeQuery(id+"F50.opExtrude","CAP_FACE",FACE,{"disambiguationData":[OSD([sQuery(id+"F49.wireOp",EDGE,"E338.MirrorCS"),sQuery(id+"F49.wireOp",EDGE,"E340.MirrorCS"),sQuery(id+"F49.wireOp",EDGE,"E341.MirrorCS"),sQuery(id+"F49.wireOp",EDGE,"E343.MirrorCS"),sQuery(id+"F49.wireOp",EDGE,"E347.MirrorCS"),sQuery(id+"F49.wireOp",EDGE,"E351.MirrorCS"),sQuery(id+"F49.wireOp",EDGE,"E352.MirrorCS"),sQuery(id+"F49.wireOp",EDGE,"E355.MirrorCS"),sQuery(id+"F49.wireOp",EDGE,"E359.MirrorCS"),sQuery(id+"F49.wireOp",EDGE,"E360.MirrorCS"),sQuery(id+"F49.wireOp",EDGE,"E364.MirrorCS"),sQuery(id+"F49.wireOp",EDGE,"E365.MirrorCS")])],"isStart":false}),makeQuery(id+"F50.opExtrude","CAP_FACE",FACE,{"disambiguationData":[OSD([sQuery(id+"F49.wireOp",EDGE,"E339.MirrorCS"),sQuery(id+"F49.wireOp",EDGE,"E342.MirrorCS"),sQuery(id+"F49.wireOp",EDGE,"E344.MirrorCS"),sQuery(id+"F49.wireOp",EDGE,"E345.MirrorCS"),sQuery(id+"F49.wireOp",EDGE,"E348.MirrorCS"),sQuery(id+"F49.wireOp",EDGE,"E350.MirrorCS"),sQuery(id+"F49.wireOp",EDGE,"E354.MirrorCS"),sQuery(id+"F49.wireOp",EDGE,"E357.MirrorCS"),sQuery(id+"F49.wireOp",EDGE,"E362.MirrorCS"),sQuery(id+"F49.wireOp",EDGE,"E363.MirrorCS"),sQuery(id+"F49.wireOp",EDGE,"E366.MirrorCS"),sQuery(id+"F49.wireOp",EDGE,"E367.MirrorCS")])],"isStart":false}),makeQuery(id+"F52.opExtrude","CAP_FACE",FACE,{"disambiguationData":[OSD([sQuery(id+"F51.wireOp",EDGE,"E369.bottom"),sQuery(id+"F51.wireOp",EDGE,"E369.top"),sQuery(id+"F51.wireOp",EDGE,"E369.left"),sQuery(id+"F51.wireOp",EDGE,"E369.right")])],"isStart":true})]}),makeQuery(id+"F54.opExtrude","CAP_FACE",FACE,{"disambiguationData":[OSD([subQ1,sQuery(id+"F53.wireOp",EDGE,"E371.top"),sQuery(id+"F53.wireOp",EDGE,"E371.left"),subQ0])],"isStart":false})]})],"blendedInto":[makeQuery(id+"F54.boolean.opBoolean","MERGE",FACE,{"derivedFrom":[makeQuery(id+"F52.boolean.opBoolean","MERGE",FACE,{"derivedFrom":[makeQuery(id+"F50.opExtrude","CAP_FACE",FACE,{"disambiguationData":[OSD([sQuery(id+"F49.wireOp",EDGE,"E319.0"),sQuery(id+"F49.wireOp",EDGE,"E319.1"),sQuery(id+"F49.wireOp",EDGE,"E319.2"),sQuery(id+"F49.wireOp",EDGE,"E319.3"),sQuery(id+"F49.wireOp",EDGE,"E319.4"),sQuery(id+"F49.wireOp",EDGE,"E319.5"),sQuery(id+"F49.wireOp",EDGE,"E320.0"),sQuery(id+"F49.wireOp",EDGE,"E320.1"),sQuery(id+"F49.wireOp",EDGE,"E320.2"),sQuery(id+"F49.wireOp",EDGE,"E320.3"),sQuery(id+"F49.wireOp",EDGE,"E320.4"),sQuery(id+"F49.wireOp",EDGE,"E320.5")])],"isStart":false}),makeQuery(id+"F50.opExtrude","CAP_FACE",FACE,{"disambiguationData":[OSD([sQuery(id+"F49.wireOp",EDGE,"E321.MirrorCS"),sQuery(id+"F49.wireOp",EDGE,"E322.MirrorCS"),sQuery(id+"F49.wireOp",EDGE,"E323.MirrorCS"),sQuery(id+"F49.wireOp",EDGE,"E325.MirrorCS"),sQuery(id+"F49.wireOp",EDGE,"E326.MirrorCS"),sQuery(id+"F49.wireOp",EDGE,"E327.MirrorCS"),sQuery(id+"F49.wireOp",EDGE,"E328.MirrorCS"),sQuery(id+"F49.wireOp",EDGE,"E329.MirrorCS"),sQuery(id+"F49.wireOp",EDGE,"E330.MirrorCS"),sQuery(id+"F49.wireOp",EDGE,"E332.MirrorCS"),sQuery(id+"F49.wireOp",EDGE,"E333.MirrorCS"),sQuery(id+"F49.wireOp",EDGE,"E334.MirrorCS")])],"isStart":false}),makeQuery(id+"F50.opExtrude","CAP_FACE",FACE,{"disambiguationData":[OSD([sQuery(id+"F49.wireOp",EDGE,"E338.MirrorCS"),sQuery(id+"F49.wireOp",EDGE,"E340.MirrorCS"),sQuery(id+"F49.wireOp",EDGE,"E341.MirrorCS"),sQuery(id+"F49.wireOp",EDGE,"E343.MirrorCS"),sQuery(id+"F49.wireOp",EDGE,"E347.MirrorCS"),sQuery(id+"F49.wireOp",EDGE,"E351.MirrorCS"),sQuery(id+"F49.wireOp",EDGE,"E352.MirrorCS"),sQuery(id+"F49.wireOp",EDGE,"E355.MirrorCS"),sQuery(id+"F49.wireOp",EDGE,"E359.MirrorCS"),sQuery(id+"F49.wireOp",EDGE,"E360.MirrorCS"),sQuery(id+"F49.wireOp",EDGE,"E364.MirrorCS"),sQuery(id+"F49.wireOp",EDGE,"E365.MirrorCS")])],"isStart":false}),makeQuery(id+"F50.opExtrude","CAP_FACE",FACE,{"disambiguationData":[OSD([sQuery(id+"F49.wireOp",EDGE,"E339.MirrorCS"),sQuery(id+"F49.wireOp",EDGE,"E342.MirrorCS"),sQuery(id+"F49.wireOp",EDGE,"E344.MirrorCS"),sQuery(id+"F49.wireOp",EDGE,"E345.MirrorCS"),sQuery(id+"F49.wireOp",EDGE,"E348.MirrorCS"),sQuery(id+"F49.wireOp",EDGE,"E350.MirrorCS"),sQuery(id+"F49.wireOp",EDGE,"E354.MirrorCS"),sQuery(id+"F49.wireOp",EDGE,"E357.MirrorCS"),sQuery(id+"F49.wireOp",EDGE,"E362.MirrorCS"),sQuery(id+"F49.wireOp",EDGE,"E363.MirrorCS"),sQuery(id+"F49.wireOp",EDGE,"E366.MirrorCS"),sQuery(id+"F49.wireOp",EDGE,"E367.MirrorCS")])],"isStart":false}),makeQuery(id+"F52.opExtrude","CAP_FACE",FACE,{"disambiguationData":[OSD([sQuery(id+"F51.wireOp",EDGE,"E369.bottom"),sQuery(id+"F51.wireOp",EDGE,"E369.top"),sQuery(id+"F51.wireOp",EDGE,"E369.left"),sQuery(id+"F51.wireOp",EDGE,"E369.right")])],"isStart":true})]}),makeQuery(id+"F54.opExtrude","CAP_FACE",FACE,{"disambiguationData":[OSD([subQ1,sQuery(id+"F53.wireOp",EDGE,"E371.top"),sQuery(id+"F53.wireOp",EDGE,"E371.left"),subQ0])],"isStart":false})]})]});}
            var Q4;
            {var subQ1=sQuery(id+"F51.wireOp",EDGE,"E369.top");Q4=makeQuery(id+"F52.boolean.opBoolean","COPY",EDGE,{"disambiguationData":[TD([makeQuery(id+"F40.boolean.opBoolean","COPY",FACE,{"derivedFrom":makeQuery(id+"F40.opExtrude","SWEPT_FACE",FACE,{"disambiguationData":[OSD([sQuery(id+"F39.wireOp",EDGE,"E256")])]})})])],"derivedFrom":makeQuery(id+"F52.opExtrude","CAP_EDGE",EDGE,{"disambiguationData":[OSD([subQ1])],"isStart":true})});}
            var Q5;
            Q5=makeQuery(id+"F52.boolean.opBoolean","INTERSECT",EDGE,{"derivedFrom":[makeQuery(id+"F40.boolean.opBoolean","COPY",FACE,{"derivedFrom":makeQuery(id+"F40.opExtrude","SWEPT_FACE",FACE,{"disambiguationData":[OSD([sQuery(id+"F39.wireOp",EDGE,"E256")])]})}),makeQuery(id+"F52.opExtrude","CAP_FACE",FACE,{"disambiguationData":[OSD([sQuery(id+"F51.wireOp",EDGE,"E369.bottom"),sQuery(id+"F51.wireOp",EDGE,"E369.top"),sQuery(id+"F51.wireOp",EDGE,"E369.left"),sQuery(id+"F51.wireOp",EDGE,"E369.right")])],"isStart":true})]});
            var Q6;
            Q6=makeQuery(id+"F52.boolean.opBoolean","INTERSECT",EDGE,{"derivedFrom":[makeQuery(id+"F40.boolean.opBoolean","COPY",FACE,{"derivedFrom":makeQuery(id+"F40.opExtrude","SWEPT_FACE",FACE,{"disambiguationData":[OSD([sQuery(id+"F39.wireOp",EDGE,"E257"),sQuery(id+"F39.wireOp",EDGE,"E258.MirrorCS")])]})}),makeQuery(id+"F52.opExtrude","CAP_FACE",FACE,{"disambiguationData":[OSD([sQuery(id+"F51.wireOp",EDGE,"E369.bottom"),sQuery(id+"F51.wireOp",EDGE,"E369.top"),sQuery(id+"F51.wireOp",EDGE,"E369.left"),sQuery(id+"F51.wireOp",EDGE,"E369.right")])],"isStart":true})]});
            var Q7;
            Q7=makeQuery(id+"F52.boolean.opBoolean","INTERSECT",EDGE,{"derivedFrom":[makeQuery(id+"F40.boolean.opBoolean","COPY",FACE,{"derivedFrom":makeQuery(id+"F40.opExtrude","SWEPT_FACE",FACE,{"disambiguationData":[OSD([sQuery(id+"F39.wireOp",EDGE,"E259.MirrorCS")])]})}),makeQuery(id+"F52.opExtrude","CAP_FACE",FACE,{"disambiguationData":[OSD([sQuery(id+"F51.wireOp",EDGE,"E369.bottom"),sQuery(id+"F51.wireOp",EDGE,"E369.top"),sQuery(id+"F51.wireOp",EDGE,"E369.left"),sQuery(id+"F51.wireOp",EDGE,"E369.right")])],"isStart":true})]});
            var Q8;
            {var subQ1=sQuery(id+"F51.wireOp",EDGE,"E369.top");Q8=makeQuery(id+"F52.boolean.opBoolean","COPY",EDGE,{"disambiguationData":[TD([makeQuery(id+"F40.boolean.opBoolean","COPY",FACE,{"derivedFrom":makeQuery(id+"F40.opExtrude","SWEPT_FACE",FACE,{"disambiguationData":[OSD([sQuery(id+"F39.wireOp",EDGE,"E259.MirrorCS")])]})})])],"derivedFrom":makeQuery(id+"F52.opExtrude","CAP_EDGE",EDGE,{"disambiguationData":[OSD([subQ1])],"isStart":true})});}
            var Q9;
            {var subQ1=sQuery(id+"F51.wireOp",EDGE,"E369.bottom");Q9=makeQuery(id+"F52.boolean.opBoolean","COPY",EDGE,{"disambiguationData":[TD([makeQuery(id+"F40.boolean.opBoolean","COPY",FACE,{"derivedFrom":makeQuery(id+"F40.opExtrude","SWEPT_FACE",FACE,{"disambiguationData":[OSD([sQuery(id+"F39.wireOp",EDGE,"E263.MirrorCS")])]})})])],"derivedFrom":makeQuery(id+"F52.opExtrude","CAP_EDGE",EDGE,{"disambiguationData":[OSD([subQ1])],"isStart":true})});}
            var Q10;
            Q10=makeQuery(id+"F52.boolean.opBoolean","INTERSECT",EDGE,{"derivedFrom":[makeQuery(id+"F40.boolean.opBoolean","COPY",FACE,{"derivedFrom":makeQuery(id+"F40.opExtrude","SWEPT_FACE",FACE,{"disambiguationData":[OSD([sQuery(id+"F39.wireOp",EDGE,"E263.MirrorCS")])]})}),makeQuery(id+"F52.opExtrude","CAP_FACE",FACE,{"disambiguationData":[OSD([sQuery(id+"F51.wireOp",EDGE,"E369.bottom"),sQuery(id+"F51.wireOp",EDGE,"E369.top"),sQuery(id+"F51.wireOp",EDGE,"E369.left"),sQuery(id+"F51.wireOp",EDGE,"E369.right")])],"isStart":true})]});
            var Q11;
            Q11=makeQuery(id+"F52.boolean.opBoolean","INTERSECT",EDGE,{"derivedFrom":[makeQuery(id+"F40.boolean.opBoolean","COPY",FACE,{"derivedFrom":makeQuery(id+"F40.opExtrude","SWEPT_FACE",FACE,{"disambiguationData":[OSD([sQuery(id+"F39.wireOp",EDGE,"E262.MirrorCS"),sQuery(id+"F39.wireOp",EDGE,"E264.MirrorCS")])]})}),makeQuery(id+"F52.opExtrude","CAP_FACE",FACE,{"disambiguationData":[OSD([sQuery(id+"F51.wireOp",EDGE,"E369.bottom"),sQuery(id+"F51.wireOp",EDGE,"E369.top"),sQuery(id+"F51.wireOp",EDGE,"E369.left"),sQuery(id+"F51.wireOp",EDGE,"E369.right")])],"isStart":true})]});
            var Q12;
            Q12=makeQuery(id+"F52.boolean.opBoolean","INTERSECT",EDGE,{"derivedFrom":[makeQuery(id+"F40.boolean.opBoolean","COPY",FACE,{"derivedFrom":makeQuery(id+"F40.opExtrude","SWEPT_FACE",FACE,{"disambiguationData":[OSD([sQuery(id+"F39.wireOp",EDGE,"E266.MirrorCS")])]})}),makeQuery(id+"F52.opExtrude","CAP_FACE",FACE,{"disambiguationData":[OSD([sQuery(id+"F51.wireOp",EDGE,"E369.bottom"),sQuery(id+"F51.wireOp",EDGE,"E369.top"),sQuery(id+"F51.wireOp",EDGE,"E369.left"),sQuery(id+"F51.wireOp",EDGE,"E369.right")])],"isStart":true})]});
            var Q13;
            {var subQ1=sQuery(id+"F51.wireOp",EDGE,"E369.bottom");Q13=makeQuery(id+"F52.boolean.opBoolean","COPY",EDGE,{"disambiguationData":[TD([makeQuery(id+"F40.boolean.opBoolean","COPY",FACE,{"derivedFrom":makeQuery(id+"F40.opExtrude","SWEPT_FACE",FACE,{"disambiguationData":[OSD([sQuery(id+"F39.wireOp",EDGE,"E266.MirrorCS")])]})})])],"derivedFrom":makeQuery(id+"F52.opExtrude","CAP_EDGE",EDGE,{"disambiguationData":[OSD([subQ1])],"isStart":true})});}
            var Q14;
            {var subQ1=sQuery(id+"F51.wireOp",EDGE,"E369.bottom");Q14=makeQuery(id+"F57.boolean.opBoolean","MERGE",EDGE,{"derivedFrom":[makeQuery(id+"F52.boolean.opBoolean","COPY",EDGE,{"disambiguationData":[TD([makeQuery(id+"F18.opExtrude","SWEPT_FACE",FACE,{"disambiguationData":[OSD([sQuery(id+"F17.wireOp",EDGE,"E197")])]})])],"derivedFrom":makeQuery(id+"F52.opExtrude","CAP_EDGE",EDGE,{"disambiguationData":[OSD([subQ1])],"isStart":true})}),makeQuery(id+"F57.opExtrude","CAP_EDGE",EDGE,{"disambiguationData":[OSD([sQuery(id+"F56.wireOp",EDGE,"E372.bottom")])],"isStart":false})]});}
            var Q15;
            Q15=makeQuery(id+"F57.opExtrude","CAP_EDGE",EDGE,{"disambiguationData":[OSD([sQuery(id+"F56.wireOp",EDGE,"E372.right")])],"isStart":false});
            var Q16;
            {var subQ0=sQuery(id+"F51.wireOp",EDGE,"E369.top");Q16=makeQuery(id+"F57.boolean.opBoolean","MERGE",EDGE,{"derivedFrom":[makeQuery(id+"F52.boolean.opBoolean","COPY",EDGE,{"disambiguationData":[TD([makeQuery(id+"F18.opExtrude","SWEPT_FACE",FACE,{"disambiguationData":[OSD([sQuery(id+"F17.wireOp",EDGE,"E197")])]})])],"derivedFrom":makeQuery(id+"F52.opExtrude","CAP_EDGE",EDGE,{"disambiguationData":[OSD([subQ0])],"isStart":true})}),makeQuery(id+"F57.opExtrude","CAP_EDGE",EDGE,{"disambiguationData":[OSD([sQuery(id+"F56.wireOp",EDGE,"E372.top")])],"isStart":false})]});}
            var Q17;
            {var subQ0=sQuery(id+"F56.wireOp",EDGE,"E372.right");var subQ1=sQuery(id+"F56.wireOp",EDGE,"E372.bottom");Q17=makeQuery(id+"F58.opChamfer","BLEND_EDGE",EDGE,{"blendedFrom":[makeQuery(id+"F57.opExtrude","SWEPT_EDGE",EDGE,{"disambiguationData":[OSD([subQ1,subQ0])]}),makeQuery(id+"F57.boolean.opBoolean","MERGE",FACE,{"derivedFrom":[makeQuery(id+"F54.boolean.opBoolean","MERGE",FACE,{"derivedFrom":[makeQuery(id+"F52.boolean.opBoolean","MERGE",FACE,{"derivedFrom":[makeQuery(id+"F50.opExtrude","CAP_FACE",FACE,{"disambiguationData":[OSD([sQuery(id+"F49.wireOp",EDGE,"E319.0"),sQuery(id+"F49.wireOp",EDGE,"E319.1"),sQuery(id+"F49.wireOp",EDGE,"E319.2"),sQuery(id+"F49.wireOp",EDGE,"E319.3"),sQuery(id+"F49.wireOp",EDGE,"E319.4"),sQuery(id+"F49.wireOp",EDGE,"E319.5"),sQuery(id+"F49.wireOp",EDGE,"E320.0"),sQuery(id+"F49.wireOp",EDGE,"E320.1"),sQuery(id+"F49.wireOp",EDGE,"E320.2"),sQuery(id+"F49.wireOp",EDGE,"E320.3"),sQuery(id+"F49.wireOp",EDGE,"E320.4"),sQuery(id+"F49.wireOp",EDGE,"E320.5")])],"isStart":false}),makeQuery(id+"F50.opExtrude","CAP_FACE",FACE,{"disambiguationData":[OSD([sQuery(id+"F49.wireOp",EDGE,"E321.MirrorCS"),sQuery(id+"F49.wireOp",EDGE,"E322.MirrorCS"),sQuery(id+"F49.wireOp",EDGE,"E323.MirrorCS"),sQuery(id+"F49.wireOp",EDGE,"E325.MirrorCS"),sQuery(id+"F49.wireOp",EDGE,"E326.MirrorCS"),sQuery(id+"F49.wireOp",EDGE,"E327.MirrorCS"),sQuery(id+"F49.wireOp",EDGE,"E328.MirrorCS"),sQuery(id+"F49.wireOp",EDGE,"E329.MirrorCS"),sQuery(id+"F49.wireOp",EDGE,"E330.MirrorCS"),sQuery(id+"F49.wireOp",EDGE,"E332.MirrorCS"),sQuery(id+"F49.wireOp",EDGE,"E333.MirrorCS"),sQuery(id+"F49.wireOp",EDGE,"E334.MirrorCS")])],"isStart":false}),makeQuery(id+"F50.opExtrude","CAP_FACE",FACE,{"disambiguationData":[OSD([sQuery(id+"F49.wireOp",EDGE,"E338.MirrorCS"),sQuery(id+"F49.wireOp",EDGE,"E340.MirrorCS"),sQuery(id+"F49.wireOp",EDGE,"E341.MirrorCS"),sQuery(id+"F49.wireOp",EDGE,"E343.MirrorCS"),sQuery(id+"F49.wireOp",EDGE,"E347.MirrorCS"),sQuery(id+"F49.wireOp",EDGE,"E351.MirrorCS"),sQuery(id+"F49.wireOp",EDGE,"E352.MirrorCS"),sQuery(id+"F49.wireOp",EDGE,"E355.MirrorCS"),sQuery(id+"F49.wireOp",EDGE,"E359.MirrorCS"),sQuery(id+"F49.wireOp",EDGE,"E360.MirrorCS"),sQuery(id+"F49.wireOp",EDGE,"E364.MirrorCS"),sQuery(id+"F49.wireOp",EDGE,"E365.MirrorCS")])],"isStart":false}),makeQuery(id+"F50.opExtrude","CAP_FACE",FACE,{"disambiguationData":[OSD([sQuery(id+"F49.wireOp",EDGE,"E339.MirrorCS"),sQuery(id+"F49.wireOp",EDGE,"E342.MirrorCS"),sQuery(id+"F49.wireOp",EDGE,"E344.MirrorCS"),sQuery(id+"F49.wireOp",EDGE,"E345.MirrorCS"),sQuery(id+"F49.wireOp",EDGE,"E348.MirrorCS"),sQuery(id+"F49.wireOp",EDGE,"E350.MirrorCS"),sQuery(id+"F49.wireOp",EDGE,"E354.MirrorCS"),sQuery(id+"F49.wireOp",EDGE,"E357.MirrorCS"),sQuery(id+"F49.wireOp",EDGE,"E362.MirrorCS"),sQuery(id+"F49.wireOp",EDGE,"E363.MirrorCS"),sQuery(id+"F49.wireOp",EDGE,"E366.MirrorCS"),sQuery(id+"F49.wireOp",EDGE,"E367.MirrorCS")])],"isStart":false}),makeQuery(id+"F52.opExtrude","CAP_FACE",FACE,{"disambiguationData":[OSD([sQuery(id+"F51.wireOp",EDGE,"E369.bottom"),sQuery(id+"F51.wireOp",EDGE,"E369.top"),sQuery(id+"F51.wireOp",EDGE,"E369.left"),sQuery(id+"F51.wireOp",EDGE,"E369.right")])],"isStart":true})]}),makeQuery(id+"F54.opExtrude","CAP_FACE",FACE,{"disambiguationData":[OSD([sQuery(id+"F53.wireOp",EDGE,"E371.bottom"),sQuery(id+"F53.wireOp",EDGE,"E371.top"),sQuery(id+"F53.wireOp",EDGE,"E371.left"),sQuery(id+"F53.wireOp",EDGE,"E371.right")])],"isStart":false})]}),makeQuery(id+"F57.opExtrude","CAP_FACE",FACE,{"disambiguationData":[OSD([subQ1,sQuery(id+"F56.wireOp",EDGE,"E372.top"),sQuery(id+"F56.wireOp",EDGE,"E372.left"),subQ0])],"isStart":false})]})],"blendedInto":[makeQuery(id+"F57.boolean.opBoolean","MERGE",FACE,{"derivedFrom":[makeQuery(id+"F54.boolean.opBoolean","MERGE",FACE,{"derivedFrom":[makeQuery(id+"F52.boolean.opBoolean","MERGE",FACE,{"derivedFrom":[makeQuery(id+"F50.opExtrude","CAP_FACE",FACE,{"disambiguationData":[OSD([sQuery(id+"F49.wireOp",EDGE,"E319.0"),sQuery(id+"F49.wireOp",EDGE,"E319.1"),sQuery(id+"F49.wireOp",EDGE,"E319.2"),sQuery(id+"F49.wireOp",EDGE,"E319.3"),sQuery(id+"F49.wireOp",EDGE,"E319.4"),sQuery(id+"F49.wireOp",EDGE,"E319.5"),sQuery(id+"F49.wireOp",EDGE,"E320.0"),sQuery(id+"F49.wireOp",EDGE,"E320.1"),sQuery(id+"F49.wireOp",EDGE,"E320.2"),sQuery(id+"F49.wireOp",EDGE,"E320.3"),sQuery(id+"F49.wireOp",EDGE,"E320.4"),sQuery(id+"F49.wireOp",EDGE,"E320.5")])],"isStart":false}),makeQuery(id+"F50.opExtrude","CAP_FACE",FACE,{"disambiguationData":[OSD([sQuery(id+"F49.wireOp",EDGE,"E321.MirrorCS"),sQuery(id+"F49.wireOp",EDGE,"E322.MirrorCS"),sQuery(id+"F49.wireOp",EDGE,"E323.MirrorCS"),sQuery(id+"F49.wireOp",EDGE,"E325.MirrorCS"),sQuery(id+"F49.wireOp",EDGE,"E326.MirrorCS"),sQuery(id+"F49.wireOp",EDGE,"E327.MirrorCS"),sQuery(id+"F49.wireOp",EDGE,"E328.MirrorCS"),sQuery(id+"F49.wireOp",EDGE,"E329.MirrorCS"),sQuery(id+"F49.wireOp",EDGE,"E330.MirrorCS"),sQuery(id+"F49.wireOp",EDGE,"E332.MirrorCS"),sQuery(id+"F49.wireOp",EDGE,"E333.MirrorCS"),sQuery(id+"F49.wireOp",EDGE,"E334.MirrorCS")])],"isStart":false}),makeQuery(id+"F50.opExtrude","CAP_FACE",FACE,{"disambiguationData":[OSD([sQuery(id+"F49.wireOp",EDGE,"E338.MirrorCS"),sQuery(id+"F49.wireOp",EDGE,"E340.MirrorCS"),sQuery(id+"F49.wireOp",EDGE,"E341.MirrorCS"),sQuery(id+"F49.wireOp",EDGE,"E343.MirrorCS"),sQuery(id+"F49.wireOp",EDGE,"E347.MirrorCS"),sQuery(id+"F49.wireOp",EDGE,"E351.MirrorCS"),sQuery(id+"F49.wireOp",EDGE,"E352.MirrorCS"),sQuery(id+"F49.wireOp",EDGE,"E355.MirrorCS"),sQuery(id+"F49.wireOp",EDGE,"E359.MirrorCS"),sQuery(id+"F49.wireOp",EDGE,"E360.MirrorCS"),sQuery(id+"F49.wireOp",EDGE,"E364.MirrorCS"),sQuery(id+"F49.wireOp",EDGE,"E365.MirrorCS")])],"isStart":false}),makeQuery(id+"F50.opExtrude","CAP_FACE",FACE,{"disambiguationData":[OSD([sQuery(id+"F49.wireOp",EDGE,"E339.MirrorCS"),sQuery(id+"F49.wireOp",EDGE,"E342.MirrorCS"),sQuery(id+"F49.wireOp",EDGE,"E344.MirrorCS"),sQuery(id+"F49.wireOp",EDGE,"E345.MirrorCS"),sQuery(id+"F49.wireOp",EDGE,"E348.MirrorCS"),sQuery(id+"F49.wireOp",EDGE,"E350.MirrorCS"),sQuery(id+"F49.wireOp",EDGE,"E354.MirrorCS"),sQuery(id+"F49.wireOp",EDGE,"E357.MirrorCS"),sQuery(id+"F49.wireOp",EDGE,"E362.MirrorCS"),sQuery(id+"F49.wireOp",EDGE,"E363.MirrorCS"),sQuery(id+"F49.wireOp",EDGE,"E366.MirrorCS"),sQuery(id+"F49.wireOp",EDGE,"E367.MirrorCS")])],"isStart":false}),makeQuery(id+"F52.opExtrude","CAP_FACE",FACE,{"disambiguationData":[OSD([sQuery(id+"F51.wireOp",EDGE,"E369.bottom"),sQuery(id+"F51.wireOp",EDGE,"E369.top"),sQuery(id+"F51.wireOp",EDGE,"E369.left"),sQuery(id+"F51.wireOp",EDGE,"E369.right")])],"isStart":true})]}),makeQuery(id+"F54.opExtrude","CAP_FACE",FACE,{"disambiguationData":[OSD([sQuery(id+"F53.wireOp",EDGE,"E371.bottom"),sQuery(id+"F53.wireOp",EDGE,"E371.top"),sQuery(id+"F53.wireOp",EDGE,"E371.left"),sQuery(id+"F53.wireOp",EDGE,"E371.right")])],"isStart":false})]}),makeQuery(id+"F57.opExtrude","CAP_FACE",FACE,{"disambiguationData":[OSD([subQ1,sQuery(id+"F56.wireOp",EDGE,"E372.top"),sQuery(id+"F56.wireOp",EDGE,"E372.left"),subQ0])],"isStart":false})]})]});}
            var Q18;
            {var subQ0=sQuery(id+"F56.wireOp",EDGE,"E372.right");var subQ1=sQuery(id+"F56.wireOp",EDGE,"E372.top");Q18=makeQuery(id+"F58.opChamfer","BLEND_EDGE",EDGE,{"blendedFrom":[makeQuery(id+"F57.opExtrude","SWEPT_EDGE",EDGE,{"disambiguationData":[OSD([subQ1,subQ0])]}),makeQuery(id+"F57.boolean.opBoolean","MERGE",FACE,{"derivedFrom":[makeQuery(id+"F54.boolean.opBoolean","MERGE",FACE,{"derivedFrom":[makeQuery(id+"F52.boolean.opBoolean","MERGE",FACE,{"derivedFrom":[makeQuery(id+"F50.opExtrude","CAP_FACE",FACE,{"disambiguationData":[OSD([sQuery(id+"F49.wireOp",EDGE,"E319.0"),sQuery(id+"F49.wireOp",EDGE,"E319.1"),sQuery(id+"F49.wireOp",EDGE,"E319.2"),sQuery(id+"F49.wireOp",EDGE,"E319.3"),sQuery(id+"F49.wireOp",EDGE,"E319.4"),sQuery(id+"F49.wireOp",EDGE,"E319.5"),sQuery(id+"F49.wireOp",EDGE,"E320.0"),sQuery(id+"F49.wireOp",EDGE,"E320.1"),sQuery(id+"F49.wireOp",EDGE,"E320.2"),sQuery(id+"F49.wireOp",EDGE,"E320.3"),sQuery(id+"F49.wireOp",EDGE,"E320.4"),sQuery(id+"F49.wireOp",EDGE,"E320.5")])],"isStart":false}),makeQuery(id+"F50.opExtrude","CAP_FACE",FACE,{"disambiguationData":[OSD([sQuery(id+"F49.wireOp",EDGE,"E321.MirrorCS"),sQuery(id+"F49.wireOp",EDGE,"E322.MirrorCS"),sQuery(id+"F49.wireOp",EDGE,"E323.MirrorCS"),sQuery(id+"F49.wireOp",EDGE,"E325.MirrorCS"),sQuery(id+"F49.wireOp",EDGE,"E326.MirrorCS"),sQuery(id+"F49.wireOp",EDGE,"E327.MirrorCS"),sQuery(id+"F49.wireOp",EDGE,"E328.MirrorCS"),sQuery(id+"F49.wireOp",EDGE,"E329.MirrorCS"),sQuery(id+"F49.wireOp",EDGE,"E330.MirrorCS"),sQuery(id+"F49.wireOp",EDGE,"E332.MirrorCS"),sQuery(id+"F49.wireOp",EDGE,"E333.MirrorCS"),sQuery(id+"F49.wireOp",EDGE,"E334.MirrorCS")])],"isStart":false}),makeQuery(id+"F50.opExtrude","CAP_FACE",FACE,{"disambiguationData":[OSD([sQuery(id+"F49.wireOp",EDGE,"E338.MirrorCS"),sQuery(id+"F49.wireOp",EDGE,"E340.MirrorCS"),sQuery(id+"F49.wireOp",EDGE,"E341.MirrorCS"),sQuery(id+"F49.wireOp",EDGE,"E343.MirrorCS"),sQuery(id+"F49.wireOp",EDGE,"E347.MirrorCS"),sQuery(id+"F49.wireOp",EDGE,"E351.MirrorCS"),sQuery(id+"F49.wireOp",EDGE,"E352.MirrorCS"),sQuery(id+"F49.wireOp",EDGE,"E355.MirrorCS"),sQuery(id+"F49.wireOp",EDGE,"E359.MirrorCS"),sQuery(id+"F49.wireOp",EDGE,"E360.MirrorCS"),sQuery(id+"F49.wireOp",EDGE,"E364.MirrorCS"),sQuery(id+"F49.wireOp",EDGE,"E365.MirrorCS")])],"isStart":false}),makeQuery(id+"F50.opExtrude","CAP_FACE",FACE,{"disambiguationData":[OSD([sQuery(id+"F49.wireOp",EDGE,"E339.MirrorCS"),sQuery(id+"F49.wireOp",EDGE,"E342.MirrorCS"),sQuery(id+"F49.wireOp",EDGE,"E344.MirrorCS"),sQuery(id+"F49.wireOp",EDGE,"E345.MirrorCS"),sQuery(id+"F49.wireOp",EDGE,"E348.MirrorCS"),sQuery(id+"F49.wireOp",EDGE,"E350.MirrorCS"),sQuery(id+"F49.wireOp",EDGE,"E354.MirrorCS"),sQuery(id+"F49.wireOp",EDGE,"E357.MirrorCS"),sQuery(id+"F49.wireOp",EDGE,"E362.MirrorCS"),sQuery(id+"F49.wireOp",EDGE,"E363.MirrorCS"),sQuery(id+"F49.wireOp",EDGE,"E366.MirrorCS"),sQuery(id+"F49.wireOp",EDGE,"E367.MirrorCS")])],"isStart":false}),makeQuery(id+"F52.opExtrude","CAP_FACE",FACE,{"disambiguationData":[OSD([sQuery(id+"F51.wireOp",EDGE,"E369.bottom"),sQuery(id+"F51.wireOp",EDGE,"E369.top"),sQuery(id+"F51.wireOp",EDGE,"E369.left"),sQuery(id+"F51.wireOp",EDGE,"E369.right")])],"isStart":true})]}),makeQuery(id+"F54.opExtrude","CAP_FACE",FACE,{"disambiguationData":[OSD([sQuery(id+"F53.wireOp",EDGE,"E371.bottom"),sQuery(id+"F53.wireOp",EDGE,"E371.top"),sQuery(id+"F53.wireOp",EDGE,"E371.left"),sQuery(id+"F53.wireOp",EDGE,"E371.right")])],"isStart":false})]}),makeQuery(id+"F57.opExtrude","CAP_FACE",FACE,{"disambiguationData":[OSD([sQuery(id+"F56.wireOp",EDGE,"E372.bottom"),subQ1,sQuery(id+"F56.wireOp",EDGE,"E372.left"),subQ0])],"isStart":false})]})],"blendedInto":[makeQuery(id+"F57.boolean.opBoolean","MERGE",FACE,{"derivedFrom":[makeQuery(id+"F54.boolean.opBoolean","MERGE",FACE,{"derivedFrom":[makeQuery(id+"F52.boolean.opBoolean","MERGE",FACE,{"derivedFrom":[makeQuery(id+"F50.opExtrude","CAP_FACE",FACE,{"disambiguationData":[OSD([sQuery(id+"F49.wireOp",EDGE,"E319.0"),sQuery(id+"F49.wireOp",EDGE,"E319.1"),sQuery(id+"F49.wireOp",EDGE,"E319.2"),sQuery(id+"F49.wireOp",EDGE,"E319.3"),sQuery(id+"F49.wireOp",EDGE,"E319.4"),sQuery(id+"F49.wireOp",EDGE,"E319.5"),sQuery(id+"F49.wireOp",EDGE,"E320.0"),sQuery(id+"F49.wireOp",EDGE,"E320.1"),sQuery(id+"F49.wireOp",EDGE,"E320.2"),sQuery(id+"F49.wireOp",EDGE,"E320.3"),sQuery(id+"F49.wireOp",EDGE,"E320.4"),sQuery(id+"F49.wireOp",EDGE,"E320.5")])],"isStart":false}),makeQuery(id+"F50.opExtrude","CAP_FACE",FACE,{"disambiguationData":[OSD([sQuery(id+"F49.wireOp",EDGE,"E321.MirrorCS"),sQuery(id+"F49.wireOp",EDGE,"E322.MirrorCS"),sQuery(id+"F49.wireOp",EDGE,"E323.MirrorCS"),sQuery(id+"F49.wireOp",EDGE,"E325.MirrorCS"),sQuery(id+"F49.wireOp",EDGE,"E326.MirrorCS"),sQuery(id+"F49.wireOp",EDGE,"E327.MirrorCS"),sQuery(id+"F49.wireOp",EDGE,"E328.MirrorCS"),sQuery(id+"F49.wireOp",EDGE,"E329.MirrorCS"),sQuery(id+"F49.wireOp",EDGE,"E330.MirrorCS"),sQuery(id+"F49.wireOp",EDGE,"E332.MirrorCS"),sQuery(id+"F49.wireOp",EDGE,"E333.MirrorCS"),sQuery(id+"F49.wireOp",EDGE,"E334.MirrorCS")])],"isStart":false}),makeQuery(id+"F50.opExtrude","CAP_FACE",FACE,{"disambiguationData":[OSD([sQuery(id+"F49.wireOp",EDGE,"E338.MirrorCS"),sQuery(id+"F49.wireOp",EDGE,"E340.MirrorCS"),sQuery(id+"F49.wireOp",EDGE,"E341.MirrorCS"),sQuery(id+"F49.wireOp",EDGE,"E343.MirrorCS"),sQuery(id+"F49.wireOp",EDGE,"E347.MirrorCS"),sQuery(id+"F49.wireOp",EDGE,"E351.MirrorCS"),sQuery(id+"F49.wireOp",EDGE,"E352.MirrorCS"),sQuery(id+"F49.wireOp",EDGE,"E355.MirrorCS"),sQuery(id+"F49.wireOp",EDGE,"E359.MirrorCS"),sQuery(id+"F49.wireOp",EDGE,"E360.MirrorCS"),sQuery(id+"F49.wireOp",EDGE,"E364.MirrorCS"),sQuery(id+"F49.wireOp",EDGE,"E365.MirrorCS")])],"isStart":false}),makeQuery(id+"F50.opExtrude","CAP_FACE",FACE,{"disambiguationData":[OSD([sQuery(id+"F49.wireOp",EDGE,"E339.MirrorCS"),sQuery(id+"F49.wireOp",EDGE,"E342.MirrorCS"),sQuery(id+"F49.wireOp",EDGE,"E344.MirrorCS"),sQuery(id+"F49.wireOp",EDGE,"E345.MirrorCS"),sQuery(id+"F49.wireOp",EDGE,"E348.MirrorCS"),sQuery(id+"F49.wireOp",EDGE,"E350.MirrorCS"),sQuery(id+"F49.wireOp",EDGE,"E354.MirrorCS"),sQuery(id+"F49.wireOp",EDGE,"E357.MirrorCS"),sQuery(id+"F49.wireOp",EDGE,"E362.MirrorCS"),sQuery(id+"F49.wireOp",EDGE,"E363.MirrorCS"),sQuery(id+"F49.wireOp",EDGE,"E366.MirrorCS"),sQuery(id+"F49.wireOp",EDGE,"E367.MirrorCS")])],"isStart":false}),makeQuery(id+"F52.opExtrude","CAP_FACE",FACE,{"disambiguationData":[OSD([sQuery(id+"F51.wireOp",EDGE,"E369.bottom"),sQuery(id+"F51.wireOp",EDGE,"E369.top"),sQuery(id+"F51.wireOp",EDGE,"E369.left"),sQuery(id+"F51.wireOp",EDGE,"E369.right")])],"isStart":true})]}),makeQuery(id+"F54.opExtrude","CAP_FACE",FACE,{"disambiguationData":[OSD([sQuery(id+"F53.wireOp",EDGE,"E371.bottom"),sQuery(id+"F53.wireOp",EDGE,"E371.top"),sQuery(id+"F53.wireOp",EDGE,"E371.left"),sQuery(id+"F53.wireOp",EDGE,"E371.right")])],"isStart":false})]}),makeQuery(id+"F57.opExtrude","CAP_FACE",FACE,{"disambiguationData":[OSD([sQuery(id+"F56.wireOp",EDGE,"E372.bottom"),subQ1,sQuery(id+"F56.wireOp",EDGE,"E372.left"),subQ0])],"isStart":false})]})]});}
            chamfer(context, id + "F61", {"entities" : qUnion([Q0, Q1, Q2, Q3, Q4, Q5, Q6, Q7, Q8, Q9, Q10, Q11, Q12, Q13, Q14, Q15, Q16, Q17, Q18]), "width" : 2.5 * mm});
        }
    });
